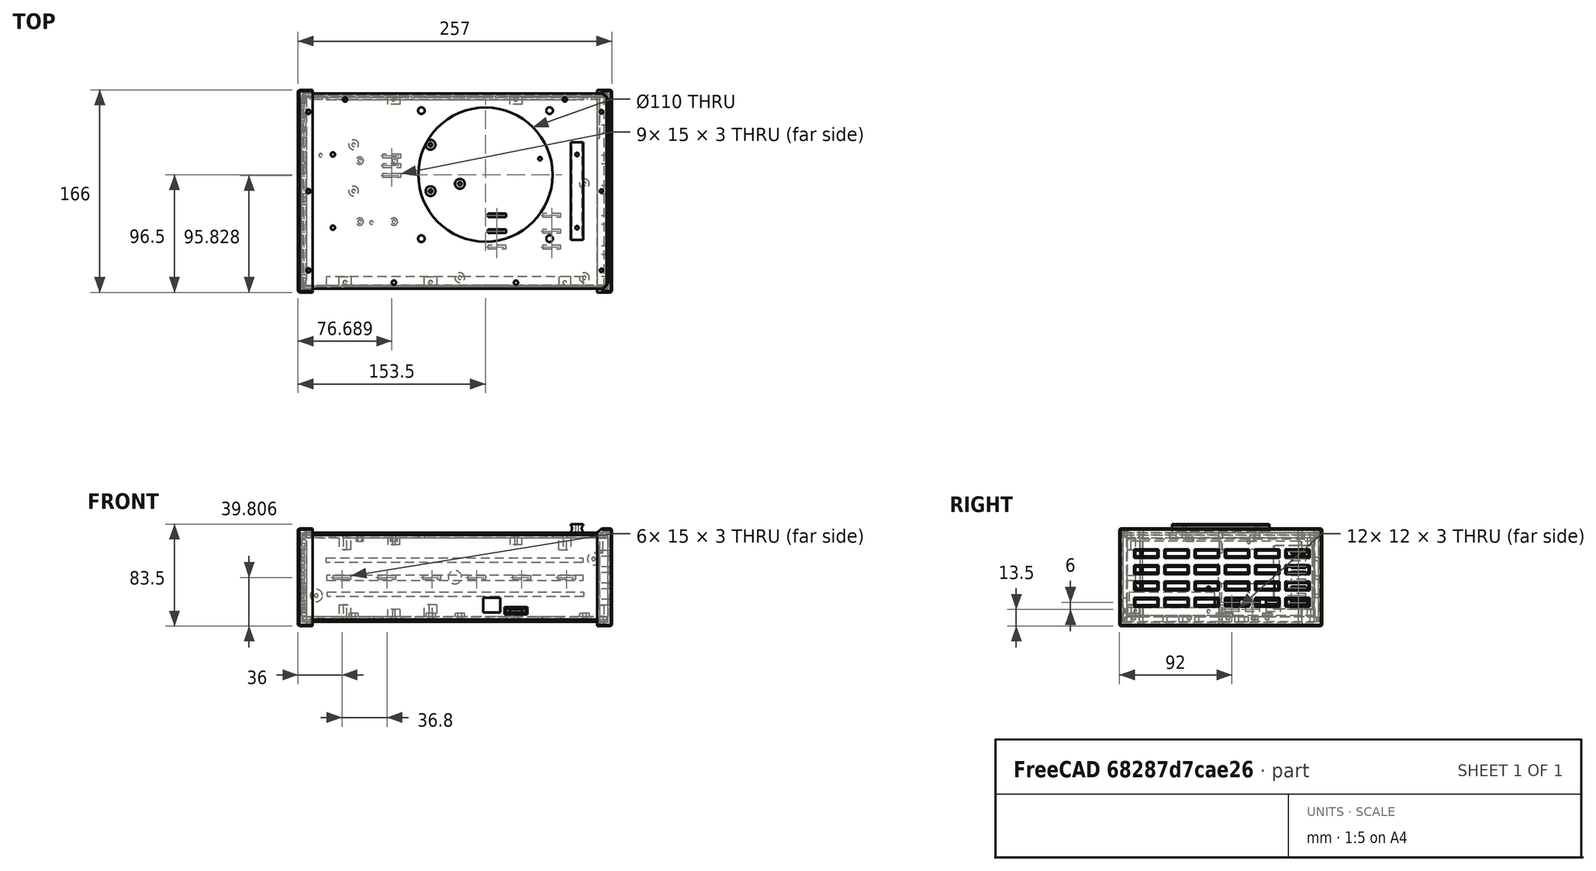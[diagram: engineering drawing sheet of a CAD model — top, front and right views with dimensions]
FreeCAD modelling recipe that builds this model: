
FCSTD DOCUMENT  (FreeCAD 0.19R)
Label: PowerBox
License: All rights reserved
LicenseURL: http://en.wikipedia.org/wiki/All_rights_reserved
objects: Sketcher::SketchObject×48, PartDesign::Pocket×28, PartDesign::Pad×18, PartDesign::Chamfer×9, Mesh::Feature×8, PartDesign::Body×7, PartDesign::Mirrored×5, PartDesign::LinearPattern×3, PartDesign::MultiTransform×2
note: 175 computed .brp shape members not serialized (recipe doc carries the construction recipe); baked Part::Feature solids carry a one-line shape summary decoded from their .brp

FEATURE [Sketcher::SketchObject] Sketch
  FullyConstrained = false
  MapMode = 5
  Support = -> [XY_Plane]
  sketch-geometry (52):
    g0: LineSegment StartX=-86.5424 StartY=49.9671 StartZ=0 EndX=-14.5424 EndY=49.9671 EndZ=0
    g1: LineSegment StartX=-14.5424 StartY=49.9671 StartZ=0 EndX=-14.5424 EndY=4.96706 EndZ=0
    g2: LineSegment StartX=-14.5424 StartY=4.96706 StartZ=0 EndX=-86.5424 EndY=4.96706 EndZ=0
    g3: LineSegment StartX=-86.5424 StartY=4.96706 StartZ=0 EndX=-86.5424 EndY=49.9671 EndZ=0
    g4: LineSegment StartX=25.4911 StartY=34.3238 StartZ=0 EndX=135.491 EndY=34.3238 EndZ=0
    g5: LineSegment StartX=135.491 StartY=34.3238 StartZ=0 EndX=135.491 EndY=-50.6762 EndZ=0
    g6: LineSegment StartX=135.491 StartY=-50.6762 StartZ=0 EndX=25.4911 EndY=-50.6762 EndZ=0
    g7: LineSegment StartX=25.4911 StartY=-50.6762 StartZ=0 EndX=25.4911 EndY=34.3238 EndZ=0
    g8: LineSegment StartX=49.4911 StartY=-35.6762 StartZ=0 EndX=61.4911 EndY=-35.6762 EndZ=0
    g9: LineSegment StartX=61.4911 StartY=-35.6762 StartZ=0 EndX=61.4911 EndY=-50.6762 EndZ=0
    g10: LineSegment StartX=61.4911 StartY=-50.6762 StartZ=0 EndX=49.4911 EndY=-50.6762 EndZ=0
    g11: LineSegment StartX=49.4911 StartY=-50.6762 StartZ=0 EndX=49.4911 EndY=-35.6762 EndZ=0
    g12: LineSegment StartX=67.9911 StartY=-35.6762 StartZ=0 EndX=82.9911 EndY=-35.6762 EndZ=0
    g13: LineSegment StartX=82.9911 StartY=-35.6762 StartZ=0 EndX=82.9911 EndY=-50.6762 EndZ=0
    g14: LineSegment StartX=82.9911 StartY=-50.6762 StartZ=0 EndX=67.9911 EndY=-50.6762 EndZ=0
    g15: LineSegment StartX=67.9911 StartY=-50.6762 StartZ=0 EndX=67.9911 EndY=-35.6762 EndZ=0
    g16: Circle CenterX=29.5661 CenterY=29.9738 CenterZ=0 NormalX=0 NormalY=0 NormalZ=1 AngleXU=0 Radius=1.75
    g17: Circle CenterX=131.416 CenterY=29.9738 CenterZ=0 NormalX=0 NormalY=0 NormalZ=1 AngleXU=0 Radius=1.75
    g18: Circle CenterX=29.5661 CenterY=-46.3262 CenterZ=0 NormalX=0 NormalY=0 NormalZ=1 AngleXU=0 Radius=1.75
    g19: Circle CenterX=131.416 CenterY=-46.3262 CenterZ=0 NormalX=0 NormalY=0 NormalZ=1 AngleXU=0 Radius=1.75
    g20: Circle CenterX=-82.0424 CenterY=46.4671 CenterZ=0 NormalX=0 NormalY=0 NormalZ=1 AngleXU=0 Radius=1.75
    g21: Circle CenterX=-19.0424 CenterY=46.4671 CenterZ=0 NormalX=0 NormalY=0 NormalZ=1 AngleXU=0 Radius=1.75
    g22: Circle CenterX=-82.0424 CenterY=8.46706 CenterZ=0 NormalX=0 NormalY=0 NormalZ=1 AngleXU=0 Radius=1.75
    g23: Circle CenterX=-19.0424 CenterY=8.46706 CenterZ=0 NormalX=0 NormalY=0 NormalZ=1 AngleXU=0 Radius=1.75
    g24: LineSegment StartX=80.4911 StartY=34.3238 StartZ=0 EndX=80.4911 EndY=-50.6762 EndZ=0
    g25: LineSegment StartX=25.4911 StartY=-8.17615 StartZ=0 EndX=135.491 EndY=-8.17615 EndZ=0
    g26: LineSegment StartX=-50.5424 StartY=4.96706 StartZ=0 EndX=-50.5424 EndY=49.9671 EndZ=0
    g27: LineSegment StartX=-86.5424 StartY=27.4671 StartZ=0 EndX=-14.5424 EndY=27.4671 EndZ=0
    g28: LineSegment StartX=-24.5424 StartY=17.4671 StartZ=0 EndX=-14.5424 EndY=17.4671 EndZ=0
    g29: LineSegment StartX=-14.5424 StartY=17.4671 StartZ=0 EndX=-14.5424 EndY=27.4671 EndZ=0
    g30: LineSegment StartX=-14.5424 StartY=27.4671 StartZ=0 EndX=-24.5424 EndY=27.4671 EndZ=0
    g31: LineSegment StartX=-24.5424 StartY=27.4671 StartZ=0 EndX=-24.5424 EndY=17.4671 EndZ=0
    g32: LineSegment StartX=-81.5424 StartY=32.4671 StartZ=0 EndX=-71.5424 EndY=32.4671 EndZ=0
    g33: LineSegment StartX=-71.5424 StartY=32.4671 StartZ=0 EndX=-71.5424 EndY=22.4671 EndZ=0
    g34: LineSegment StartX=-71.5424 StartY=22.4671 StartZ=0 EndX=-81.5424 EndY=22.4671 EndZ=0
    g35: LineSegment StartX=-81.5424 StartY=22.4671 StartZ=0 EndX=-81.5424 EndY=32.4671 EndZ=0
    g36: LineSegment StartX=-100.377 StartY=89.1721 StartZ=0 EndX=139.623 EndY=89.1721 EndZ=0
    g37: LineSegment StartX=139.623 StartY=89.1721 StartZ=0 EndX=139.623 EndY=59.1721 EndZ=0
    g38: LineSegment StartX=139.623 StartY=59.1721 StartZ=0 EndX=-100.377 EndY=59.1721 EndZ=0
    g39: LineSegment StartX=-100.377 StartY=59.1721 StartZ=0 EndX=-100.377 EndY=89.1721 EndZ=0
    g40: LineSegment StartX=-96.5075 StartY=-1.10795 StartZ=0 EndX=3.49248 EndY=-1.10795 EndZ=0
    g41: LineSegment StartX=3.49248 StartY=-1.10795 StartZ=0 EndX=3.49248 EndY=-54.108 EndZ=0
    g42: LineSegment StartX=3.49248 StartY=-54.108 StartZ=0 EndX=-96.5075 EndY=-54.108 EndZ=0
    g43: LineSegment StartX=-96.5075 StartY=-54.108 StartZ=0 EndX=-96.5075 EndY=-1.10795 EndZ=0
    g44: LineSegment StartX=40.4911 StartY=31.3238 StartZ=0 EndX=120.491 EndY=31.3238 EndZ=0
    g45: LineSegment StartX=120.491 StartY=31.3238 StartZ=0 EndX=120.491 EndY=21.3238 EndZ=0
    g46: LineSegment StartX=120.491 StartY=21.3238 StartZ=0 EndX=40.4911 EndY=21.3238 EndZ=0
    g47: LineSegment StartX=40.4911 StartY=21.3238 StartZ=0 EndX=40.4911 EndY=31.3238 EndZ=0
    g48: LineSegment StartX=-125 StartY=80 StartZ=0 EndX=125 EndY=80 EndZ=0
    g49: LineSegment StartX=125 StartY=80 StartZ=0 EndX=125 EndY=-80 EndZ=0
    g50: LineSegment StartX=125 StartY=-80 StartZ=0 EndX=-125 EndY=-80 EndZ=0
    g51: LineSegment StartX=-125 StartY=-80 StartZ=0 EndX=-125 EndY=80 EndZ=0
  constraints (138):
    c: Coincident(g0,g1)
    c: Coincident(g1,g2)
    c: Coincident(g2,g3)
    c: Coincident(g3,g0)
    c: Horizontal(g0)
    c: Horizontal(g2)
    c: Vertical(g1)
    c: Vertical(g3)
    c: Distance(g0) = 72
    c: Distance(g1) = 45
    c: Coincident(g4,g5)
    c: Coincident(g5,g6)
    c: Coincident(g6,g7)
    c: Coincident(g7,g4)
    c: Horizontal(g4)
    c: Horizontal(g6)
    c: Vertical(g5)
    c: Vertical(g7)
    c: Distance(g4) = 110
    c: Distance(g5) = 85
    c: Coincident(g8,g9)
    c: Coincident(g9,g10)
    c: Coincident(g10,g11)
    c: Coincident(g11,g8)
    c: Horizontal(g8)
    c: Horizontal(g10)
    c: Vertical(g9)
    c: Vertical(g11)
    c: Coincident(g12,g13)
    c: Coincident(g13,g14)
    c: Coincident(g14,g15)
    c: Coincident(g15,g12)
    c: Horizontal(g12)
    c: Horizontal(g14)
    c: Vertical(g13)
    c: Vertical(g15)
    c: Distance(g6,g10) = 24
    c: Distance(g9,g6) = 36
    c: PointOnObject(g9,g6)
    c: DistanceX(g6,g14) = 42.5
    c: PointOnObject(g14,g6)
    c: Distance(g13,g6) = 57.5
    c: Equal(g9,g15)
    c: Distance(g13) = 15
    c: Diameter(g20) = 3.5
    c: Equal(g20,g22)
    c: Equal(g20,g21)
    c: Equal(g20,g23)
    c: Equal(g20,g16)
    c: Equal(g20,g18)
    c: Equal(g20,g17)
    c: Equal(g20,g19)
    c: PointOnObject(g24,g6)
    c: Vertical(g24)
    c: PointOnObject(g25,g7)
    c: Horizontal(g25)
    c: PointOnObject(g26,g2)
    c: PointOnObject(g27,g3)
    c: Horizontal(g27)
    c: Vertical(g26)
    c: Symmetric(g0,g0,g26)
    c: Symmetric(g0,g1,g27)
    c: Symmetric(g5,g4,g25)
    c: Symmetric(g4,g4,g24)
    c: Symmetric(g17,g16,g24)
    c: Distance(g16,g17) = 101.85
    c: Symmetric(g19,g17,g25)
    c: Distance(g17,g19) = 76.3
    c: DistanceX(g16,g18) = 0
    c: DistanceY(g19,g18) = 0
    c: Symmetric(g20,g21,g26)
    c: Symmetric(g23,g21,g27)
    c: Symmetric(g22,g20,g27)
    c: Distance(g21,g23) = 38
    c: Distance(g21,g20) = 63
    c: Coincident(g28,g29)
    c: Coincident(g29,g30)
    c: Coincident(g30,g31)
    c: Coincident(g31,g28)
    c: Horizontal(g28)
    c: Horizontal(g30)
    c: Vertical(g29)
    c: Vertical(g31)
    c: Coincident(g32,g33)
    c: Coincident(g33,g34)
    c: Coincident(g34,g35)
    c: Coincident(g35,g32)
    c: Horizontal(g32)
    c: Horizontal(g34)
    c: Vertical(g35)
    c: Symmetric(g33,g32,g27)
    c: Distance(g33) = 10
    c: Distance(g32) = 10
    c: Distance(g32,g3) = 5
    c: Coincident(g29,g27)
    c: Distance(g28) = 10
    c: Distance(g31) = 10
    c: Coincident(g36,g37)
    c: Coincident(g37,g38)
    c: Coincident(g38,g39)
    c: Coincident(g39,g36)
    c: Horizontal(g36)
    c: Horizontal(g38)
    c: Vertical(g37)
    c: Vertical(g39)
    c: Distance(g36) = 240
    c: Distance(g37) = 30
    c: Coincident(g40,g41)
    c: Coincident(g41,g42)
    c: Coincident(g42,g43)
    c: Coincident(g43,g40)
    c: Horizontal(g40)
    c: Horizontal(g42)
    c: Vertical(g41)
    c: Vertical(g43)
    c: Distance(g40) = 100
    c: Distance(g41) = 53
    c: Coincident(g44,g45)
    c: Coincident(g45,g46)
    c: Coincident(g46,g47)
    c: Coincident(g47,g44)
    c: Horizontal(g46)
    c: Vertical(g45)
    c: Vertical(g47)
    c: Symmetric(g44,g44,g24)
    c: Distance(g45) = 10
    c: Distance(g44) = 80
    c: Distance(g44,g4) = 3
    c: Coincident(g48,g49)
    c: Coincident(g49,g50)
    c: Coincident(g50,g51)
    c: Coincident(g51,g48)
    c: Horizontal(g50)
    c: Vertical(g49)
    c: Distance(g49) = 160
    c: Distance(g48) = 250
    c: Symmetric(g48,g48,g-2)
    c: Symmetric(g50,g48,g-1)
FEATURE [PartDesign::Pad] Pad
  Direction = (1,1,1)
  Length = 4
  Length2 = 100
  Profile = -> Sketch
  Type = 0
FEATURE [Sketcher::SketchObject] Sketch001
  FullyConstrained = false
  MapMode = 5
  Placement = pos=(0,0,4) rot=(0,0,1;0rad)
  Support = -> [Pad]
  sketch-geometry (60):
    g0: LineSegment StartX=-87.5 StartY=41.4585 StartZ=0 EndX=-15.5 EndY=41.4585 EndZ=0
    g1: LineSegment StartX=-15.5 StartY=41.4585 StartZ=0 EndX=-15.5 EndY=-3.45847 EndZ=0
    g2: LineSegment StartX=-15.5 StartY=-3.45847 StartZ=0 EndX=-87.5 EndY=-3.45847 EndZ=0
    g3: LineSegment StartX=-87.5 StartY=-3.45847 StartZ=0 EndX=-87.5 EndY=41.4585 EndZ=0
    g4: LineSegment StartX=0 StartY=10 StartZ=0 EndX=110 EndY=10 EndZ=0
    g5: LineSegment StartX=110 StartY=10 StartZ=0 EndX=110 EndY=-75 EndZ=0
    g6: LineSegment StartX=110 StartY=-75 StartZ=0 EndX=0 EndY=-75 EndZ=0
    g7: LineSegment StartX=0 StartY=-75 StartZ=0 EndX=0 EndY=10 EndZ=0
    g8: LineSegment StartX=24 StartY=-60 StartZ=0 EndX=36 EndY=-60 EndZ=0
    g9: LineSegment StartX=36 StartY=-60 StartZ=0 EndX=36 EndY=-75 EndZ=0
    g10: LineSegment StartX=36 StartY=-75 StartZ=0 EndX=24 EndY=-75 EndZ=0
    g11: LineSegment StartX=24 StartY=-75 StartZ=0 EndX=24 EndY=-60 EndZ=0
    g12: LineSegment StartX=42.5 StartY=-60 StartZ=0 EndX=57.5 EndY=-60 EndZ=0
    g13: LineSegment StartX=57.5 StartY=-60 StartZ=0 EndX=57.5 EndY=-75 EndZ=0
    g14: LineSegment StartX=57.5 StartY=-75 StartZ=0 EndX=42.5 EndY=-75 EndZ=0
    g15: LineSegment StartX=42.5 StartY=-75 StartZ=0 EndX=42.5 EndY=-60 EndZ=0
    g16: Circle CenterX=4 CenterY=6 CenterZ=0 NormalX=0 NormalY=0 NormalZ=1 AngleXU=0 Radius=1.75
    g17: Circle CenterX=106 CenterY=6 CenterZ=0 NormalX=0 NormalY=0 NormalZ=1 AngleXU=0 Radius=1.75
    g18: Circle CenterX=4 CenterY=-71 CenterZ=0 NormalX=0 NormalY=0 NormalZ=1 AngleXU=0 Radius=1.75
    g19: Circle CenterX=106 CenterY=-71 CenterZ=0 NormalX=0 NormalY=0 NormalZ=1 AngleXU=0 Radius=1.75
    g20: Circle CenterX=-83 CenterY=38 CenterZ=0 NormalX=0 NormalY=0 NormalZ=1 AngleXU=0 Radius=1.75
    g21: Circle CenterX=-20 CenterY=38 CenterZ=0 NormalX=0 NormalY=0 NormalZ=1 AngleXU=0 Radius=1.75
    g22: Circle CenterX=-83 CenterY=-3.5e-15 CenterZ=0 NormalX=0 NormalY=0 NormalZ=1 AngleXU=0 Radius=1.75
    g23: Circle CenterX=-20 CenterY=0 CenterZ=0 NormalX=0 NormalY=0 NormalZ=1 AngleXU=0 Radius=1.75
    g24: LineSegment StartX=55 StartY=10 StartZ=0 EndX=55 EndY=-75 EndZ=0
    g25: LineSegment StartX=3.9e-15 StartY=-32.5 StartZ=0 EndX=110 EndY=-32.5 EndZ=0
    g26: LineSegment StartX=-51.5 StartY=-3.45847 StartZ=0 EndX=-51.5 EndY=41.4585 EndZ=0
    g27: LineSegment StartX=-87.5 StartY=19 StartZ=0 EndX=-15.5 EndY=19 EndZ=0
    g28: LineSegment StartX=-25.5 StartY=9 StartZ=0 EndX=-15.5 EndY=9 EndZ=0
    g29: LineSegment StartX=-15.5 StartY=9 StartZ=0 EndX=-15.5 EndY=19 EndZ=0
    g30: LineSegment StartX=-15.5 StartY=19 StartZ=0 EndX=-25.5 EndY=19 EndZ=0
    g31: LineSegment StartX=-25.5 StartY=19 StartZ=0 EndX=-25.5 EndY=9 EndZ=0
    g32: LineSegment StartX=-82.5 StartY=24 StartZ=0 EndX=-72.5 EndY=24 EndZ=0
    g33: LineSegment StartX=-72.5 StartY=24 StartZ=0 EndX=-72.5 EndY=14 EndZ=0
    g34: LineSegment StartX=-72.5 StartY=14 StartZ=0 EndX=-82.5 EndY=14 EndZ=0
    g35: LineSegment StartX=-82.5 StartY=14 StartZ=0 EndX=-82.5 EndY=24 EndZ=0
    g36: LineSegment StartX=-120.694 StartY=75.1603 StartZ=0 EndX=119.306 EndY=75.1603 EndZ=0
    g37: LineSegment StartX=119.306 StartY=75.1603 StartZ=0 EndX=119.306 EndY=45.1603 EndZ=0
    g38: LineSegment StartX=119.306 StartY=45.1603 StartZ=0 EndX=-120.694 EndY=45.1603 EndZ=0
    g39: LineSegment StartX=-120.694 StartY=45.1603 StartZ=0 EndX=-120.694 EndY=75.1603 EndZ=0
    g40: LineSegment StartX=-121.323 StartY=-10.2354 StartZ=0 EndX=-21.3228 EndY=-10.2354 EndZ=0
    g41: LineSegment StartX=-21.3228 StartY=-10.2354 StartZ=0 EndX=-21.3228 EndY=-63.2354 EndZ=0
    g42: LineSegment StartX=-21.3228 StartY=-63.2354 StartZ=0 EndX=-121.323 EndY=-63.2354 EndZ=0
    g43: LineSegment StartX=-121.323 StartY=-63.2354 StartZ=0 EndX=-121.323 EndY=-10.2354 EndZ=0
    g44: LineSegment StartX=15 StartY=7 StartZ=0 EndX=95 EndY=7 EndZ=0
    g45: LineSegment StartX=95 StartY=7 StartZ=0 EndX=95 EndY=-3 EndZ=0
    g46: LineSegment StartX=95 StartY=-3 StartZ=0 EndX=15 EndY=-3 EndZ=0
    g47: LineSegment StartX=15 StartY=-3 StartZ=0 EndX=15 EndY=7 EndZ=0
    g48: LineSegment StartX=-125.107 StartY=95.65 StartZ=0 EndX=124.893 EndY=95.65 EndZ=0
    g49: LineSegment StartX=124.893 StartY=95.65 StartZ=0 EndX=124.893 EndY=-80.1453 EndZ=0
    g50: LineSegment StartX=124.893 StartY=-80.1453 StartZ=0 EndX=-125.107 EndY=-80.1453 EndZ=0
    g51: LineSegment StartX=-125.107 StartY=-80.1453 StartZ=0 EndX=-125.107 EndY=95.65 EndZ=0
    g52: Circle CenterX=4 CenterY=6 CenterZ=0 NormalX=0 NormalY=0 NormalZ=1 AngleXU=0 Radius=4
    g53: Circle CenterX=106 CenterY=6 CenterZ=0 NormalX=0 NormalY=0 NormalZ=1 AngleXU=0 Radius=4
    g54: Circle CenterX=106 CenterY=-71 CenterZ=0 NormalX=0 NormalY=0 NormalZ=1 AngleXU=0 Radius=4
    g55: Circle CenterX=4 CenterY=-71 CenterZ=0 NormalX=0 NormalY=0 NormalZ=1 AngleXU=0 Radius=4
    g56: Circle CenterX=-83 CenterY=38 CenterZ=0 NormalX=0 NormalY=0 NormalZ=1 AngleXU=0 Radius=4
    g57: Circle CenterX=-20 CenterY=38 CenterZ=0 NormalX=0 NormalY=0 NormalZ=1 AngleXU=0 Radius=4
    g58: Circle CenterX=-20 CenterY=0 CenterZ=0 NormalX=0 NormalY=0 NormalZ=1 AngleXU=0 Radius=4
    g59: Circle CenterX=-83 CenterY=-3.5e-15 CenterZ=0 NormalX=0 NormalY=0 NormalZ=1 AngleXU=0 Radius=4
  constraints (156):
    c: Coincident(g0,g1)
    c: Coincident(g1,g2)
    c: Coincident(g2,g3)
    c: Coincident(g3,g0)
    c: Horizontal(g0)
    c: Horizontal(g2)
    c: Vertical(g1)
    c: Vertical(g3)
    c: Distance(g0) = 72
    c: Coincident(g4,g5)
    c: Coincident(g5,g6)
    c: Coincident(g6,g7)
    c: Coincident(g7,g4)
    c: Horizontal(g4)
    c: Horizontal(g6)
    c: Vertical(g5)
    c: Vertical(g7)
    c: Distance(g4) = 110
    c: Distance(g5) = 85
    c: Coincident(g8,g9)
    c: Coincident(g9,g10)
    c: Coincident(g10,g11)
    c: Coincident(g11,g8)
    c: Horizontal(g8)
    c: Horizontal(g10)
    c: Vertical(g9)
    c: Vertical(g11)
    c: Coincident(g12,g13)
    c: Coincident(g13,g14)
    c: Coincident(g14,g15)
    c: Coincident(g15,g12)
    c: Horizontal(g12)
    c: Horizontal(g14)
    c: Vertical(g13)
    c: Vertical(g15)
    c: Distance(g6,g10) = 24
    c: Distance(g9,g6) = 36
    c: PointOnObject(g9,g6)
    c: DistanceX(g6,g14) = 42.5
    c: PointOnObject(g14,g6)
    c: Distance(g13,g6) = 57.5
    c: Equal(g9,g15)
    c: Distance(g13) = 15
    c: Diameter(g20) = 3.5
    c: Equal(g20,g22)
    c: Equal(g20,g21)
    c: Equal(g20,g23)
    c: Equal(g20,g16)
    c: Equal(g20,g18)
    c: Equal(g20,g17)
    c: Equal(g20,g19)
    c: PointOnObject(g24,g6)
    c: Vertical(g24)
    c: PointOnObject(g25,g7)
    c: Horizontal(g25)
    c: PointOnObject(g26,g2)
    c: PointOnObject(g27,g3)
    c: Horizontal(g27)
    c: Vertical(g26)
    c: Symmetric(g0,g0,g26)
    c: Symmetric(g0,g1,g27)
    c: Symmetric(g5,g4,g25)
    c: Symmetric(g4,g4,g24)
    c: Symmetric(g17,g16,g24)
    c: Distance(g16,g17) = 102
    c: Symmetric(g19,g17,g25)
    c: DistanceX(g16,g18) = 0
    c: DistanceY(g19,g18) = 0
    c: Symmetric(g20,g21,g26)
    c: Symmetric(g23,g21,g27)
    c: Symmetric(g22,g20,g27)
    c: Distance(g21,g23) = 38
    c: Distance(g21,g20) = 63
    c: Coincident(g28,g29)
    c: Coincident(g29,g30)
    c: Coincident(g30,g31)
    c: Coincident(g31,g28)
    c: Horizontal(g28)
    c: Horizontal(g30)
    c: Vertical(g29)
    c: Vertical(g31)
    c: Coincident(g32,g33)
    c: Coincident(g33,g34)
    c: Coincident(g34,g35)
    c: Coincident(g35,g32)
    c: Horizontal(g32)
    c: Horizontal(g34)
    c: Vertical(g35)
    c: Symmetric(g33,g32,g27)
    c: Distance(g33) = 10
    c: Distance(g32) = 10
    c: Distance(g32,g3) = 5
    c: Coincident(g29,g27)
    c: Distance(g28) = 10
    c: Distance(g31) = 10
    c: Coincident(g36,g37)
    c: Coincident(g37,g38)
    c: Coincident(g38,g39)
    c: Coincident(g39,g36)
    c: Horizontal(g36)
    c: Horizontal(g38)
    c: Vertical(g37)
    c: Vertical(g39)
    c: Distance(g36) = 240
    c: Distance(g37) = 30
    c: Coincident(g40,g41)
    c: Coincident(g41,g42)
    c: Coincident(g42,g43)
    c: Coincident(g43,g40)
    c: Horizontal(g40)
    c: Horizontal(g42)
    c: Vertical(g41)
    c: Vertical(g43)
    c: Distance(g40) = 100
    c: Distance(g41) = 53
    c: Coincident(g44,g45)
    c: Coincident(g45,g46)
    c: Coincident(g46,g47)
    c: Coincident(g47,g44)
    c: Horizontal(g46)
    c: Vertical(g45)
    c: Vertical(g47)
    c: Symmetric(g44,g44,g24)
    c: Distance(g45) = 10
    c: Distance(g44) = 80
    c: Distance(g44,g4) = 3
    c: Coincident(g48,g49)
    c: Coincident(g49,g50)
    c: Coincident(g50,g51)
    c: Coincident(g51,g48)
    c: Horizontal(g48)
    c: Horizontal(g50)
    c: Vertical(g49)
    c: Vertical(g51)
    c: Distance(g48) = 250
    c: Coincident(g52,g16)
    c: Coincident(g53,g17)
    c: Coincident(g54,g19)
    c: Coincident(g55,g18)
    c: Coincident(g56,g20)
    c: Coincident(g57,g21)
    c: Coincident(g58,g23)
    c: Coincident(g59,g22)
    c: Diameter(g54) = 8
    c: Equal(g54,g53)
    c: Equal(g54,g52)
    c: Equal(g54,g55)
    c: Equal(g54,g58)
    c: Equal(g54,g57)
    c: Equal(g54,g56)
    c: Equal(g54,g59)
    c: DistanceY(g5) = -75
    c: DistanceX(g5) = 110
    c: DistanceX(g57) = -20
    c: Distance(g53,g54) = 77
    c: PointOnObject(g58,g-1)
FEATURE [Sketcher::SketchObject] Sketch003  label="reference"
  FullyConstrained = false
  MapMode = 5
  Placement = pos=(0,0,0) rot=(0.57735,0.57735,0.57735;2.0944rad)
  Support = -> [YZ_Plane001]
  sketch-geometry (4):
    g0: LineSegment StartX=-80.0312 StartY=59.7173 StartZ=0 EndX=-51.0312 EndY=59.7173 EndZ=0
    g1: LineSegment StartX=-51.0312 StartY=59.7173 StartZ=0 EndX=-51.0312 EndY=11.7173 EndZ=0
    g2: LineSegment StartX=-51.0312 StartY=11.7173 StartZ=0 EndX=-80.0312 EndY=11.7173 EndZ=0
    g3: LineSegment StartX=-80.0312 StartY=11.7173 StartZ=0 EndX=-80.0312 EndY=59.7173 EndZ=0
  constraints (10):
    c: Coincident(g0,g1)
    c: Coincident(g1,g2)
    c: Coincident(g2,g3)
    c: Coincident(g3,g0)
    c: Horizontal(g0)
    c: Horizontal(g2)
    c: Vertical(g1)
    c: Vertical(g3)
    c: Distance(g0) = 29
    c: Distance(g3) = 48
FEATURE [PartDesign::Pad] Pad001
  BaseFeature = -> Pad
  Direction = (1,1,1)
  Length = 3
  Length2 = 100
  Profile = -> Sketch001
  Type = 0
FEATURE [Sketcher::SketchObject] Sketch002
  ExternalGeometry = -> [Pad001]
  FullyConstrained = true
  MapMode = 5
  Placement = pos=(0,0,7) rot=(0,0,1;0rad)
  sketch-geometry (8):
    g0: Circle CenterX=-83 CenterY=38 CenterZ=0 NormalX=0 NormalY=0 NormalZ=1 AngleXU=0 Radius=1.4
    g1: Circle CenterX=-20 CenterY=38 CenterZ=0 NormalX=0 NormalY=0 NormalZ=1 AngleXU=0 Radius=1.4
    g2: Circle CenterX=-83 CenterY=-3.5e-15 CenterZ=0 NormalX=0 NormalY=0 NormalZ=1 AngleXU=0 Radius=1.4
    g3: Circle CenterX=-20 CenterY=0 CenterZ=0 NormalX=0 NormalY=0 NormalZ=1 AngleXU=0 Radius=1.4
    g4: Circle CenterX=4 CenterY=6 CenterZ=0 NormalX=0 NormalY=0 NormalZ=1 AngleXU=0 Radius=1.4
    g5: Circle CenterX=106 CenterY=6 CenterZ=0 NormalX=0 NormalY=0 NormalZ=1 AngleXU=0 Radius=1.4
    g6: Circle CenterX=106 CenterY=-71 CenterZ=0 NormalX=0 NormalY=0 NormalZ=1 AngleXU=0 Radius=1.4
    g7: Circle CenterX=4 CenterY=-71 CenterZ=0 NormalX=0 NormalY=0 NormalZ=1 AngleXU=0 Radius=1.4
  constraints (12):
    c: Diameter(g0) = 2.8
    c: Equal(g0,g2)
    c: Equal(g0,g1)
    c: Equal(g0, g3-g7) x5
    c: Coincident(g7,g-10)
    c: Coincident(g4,g-7)
    c: Coincident(g5,g-8)
    c: Coincident(g6,g-9)
    c: Coincident(g-3,g0)
    c: Coincident(g2,g-6)
    c: Coincident(g1,g-4)
    c: Coincident(g3,g-5)
FEATURE [PartDesign::Pocket] Pocket
  BaseFeature = -> Pad001
  Length = 5
  Length2 = 100
  Profile = -> Sketch002
  Type = 0
FEATURE [Sketcher::SketchObject] Sketch004  label="MainPad"
  FullyConstrained = true
  MapMode = 5
  Placement = pos=(0,0,0) rot=(0.57735,0.57735,0.57735;2.0944rad)
  Support = -> [YZ_Plane001]
  sketch-geometry (4):
    g0: LineSegment StartX=-83 StartY=40 StartZ=0 EndX=83 EndY=40 EndZ=0
    g1: LineSegment StartX=83 StartY=40 StartZ=0 EndX=83 EndY=-40 EndZ=0
    g2: LineSegment StartX=83 StartY=-40 StartZ=0 EndX=-83 EndY=-40 EndZ=0
    g3: LineSegment StartX=-83 StartY=-40 StartZ=0 EndX=-83 EndY=40 EndZ=0
  constraints (10):
    c: Coincident(g0,g1)
    c: Coincident(g1,g2)
    c: Coincident(g2,g3)
    c: Coincident(g3,g0)
    c: Horizontal(g0)
    c: Vertical(g3)
    c: Symmetric(g1,g2,g-2)
    c: Distance(g2) = 166
    c: Distance(g1) = 80
    c: Symmetric(g1,g0,g-1)
FEATURE [PartDesign::Pad] Pad002
  Direction = (1,1,1)
  Length = 12
  Length2 = 100
  Placement = pos=(0,0,0) rot=(0.57735,0.57735,0.57735;2.0944rad)
  Profile = -> Sketch004
  Type = 0
FEATURE [Sketcher::SketchObject] Sketch005  label="MainPocket"
  FullyConstrained = true
  MapMode = 5
  Placement = pos=(0,0,0) rot=(0.57735,0.57735,-0.57735;4.18879rad)
  Support = -> [Pad002]
  sketch-geometry (8):
    g0: LineSegment StartX=-80.25 StartY=36.75 StartZ=0 EndX=80.25 EndY=36.75 EndZ=0
    g1: LineSegment StartX=80.25 StartY=36.75 StartZ=0 EndX=80.25 EndY=-36.75 EndZ=0
    g2: LineSegment StartX=80.25 StartY=-36.75 StartZ=0 EndX=-80.25 EndY=-36.75 EndZ=0
    g3: LineSegment StartX=-80.25 StartY=-36.75 StartZ=0 EndX=-80.25 EndY=36.75 EndZ=0
    g4: LineSegment StartX=-77 StartY=32 StartZ=0 EndX=77 EndY=32 EndZ=0
    g5: LineSegment StartX=77 StartY=32 StartZ=0 EndX=77 EndY=-32 EndZ=0
    g6: LineSegment StartX=77 StartY=-32 StartZ=0 EndX=-77 EndY=-32 EndZ=0
    g7: LineSegment StartX=-77 StartY=-32 StartZ=0 EndX=-77 EndY=32 EndZ=0
  constraints (22):
    c: Coincident(g0,g1)
    c: Coincident(g1,g2)
    c: Coincident(g2,g3)
    c: Coincident(g3,g0)
    c: Horizontal(g0)
    c: Horizontal(g2)
    c: Vertical(g1)
    c: Vertical(g3)
    c: Distance(g0) = 160.5
    c: Distance(g1) = 73.5
    c: Symmetric(g0,g2,g-1)
    c: Coincident(g4,g5)
    c: Coincident(g5,g6)
    c: Coincident(g6,g7)
    c: Coincident(g7,g4)
    c: Horizontal(g4)
    c: Horizontal(g6)
    c: Vertical(g5)
    c: Vertical(g7)
    c: Distance(g7) = 64
    c: Symmetric(g4,g6,g-1)
    c: Distance(g6) = 154
FEATURE [PartDesign::Pocket] Pocket001
  BaseFeature = -> Pad002
  Length = 9
  Length2 = 100
  Placement = pos=(0,0,0) rot=(0.57735,0.57735,0.57735;2.0944rad)
  Profile = -> Sketch005
  Type = 0
FEATURE [Sketcher::SketchObject] Sketch006  label="body"
  FullyConstrained = true
  MapMode = 5
  Placement = pos=(0,0,0) rot=(1,0,0;1.5708rad)
  Support = -> [XZ_Plane002]
  sketch-geometry (4):
    g0: LineSegment StartX=-125 StartY=32.5 StartZ=0 EndX=125 EndY=32.5 EndZ=0
    g1: LineSegment StartX=125 StartY=32.5 StartZ=0 EndX=125 EndY=-32.5 EndZ=0
    g2: LineSegment StartX=125 StartY=-32.5 StartZ=0 EndX=-125 EndY=-32.5 EndZ=0
    g3: LineSegment StartX=-125 StartY=-32.5 StartZ=0 EndX=-125 EndY=32.5 EndZ=0
  constraints (11):
    c: Coincident(g0,g1)
    c: Coincident(g1,g2)
    c: Coincident(g2,g3)
    c: Coincident(g3,g0)
    c: Horizontal(g0)
    c: Vertical(g1)
    c: Vertical(g3)
    c: Distance(g2) = 250
    c: Distance(g1) = 65
    c: Symmetric(g2,g0,g-1)
    c: Equal(g3,g1)
FEATURE [PartDesign::Pad] Pad003
  Direction = (1,1,1)
  Length = 3
  Length2 = 100
  Placement = pos=(0,0,0) rot=(1,0,0;1.5708rad)
  Profile = -> Sketch006
  Type = 0
FEATURE [Sketcher::SketchObject] Sketch007
  FullyConstrained = true
  MapMode = 5
  Placement = pos=(0,0,0) rot=(1,0,0;1.5708rad)
  Support = -> [XZ_Plane003]
  sketch-geometry (4):
    g0: LineSegment StartX=-125 StartY=32.5 StartZ=0 EndX=125 EndY=32.5 EndZ=0
    g1: LineSegment StartX=125 StartY=32.5 StartZ=0 EndX=125 EndY=-32.5 EndZ=0
    g2: LineSegment StartX=125 StartY=-32.5 StartZ=0 EndX=-125 EndY=-32.5 EndZ=0
    g3: LineSegment StartX=-125 StartY=-32.5 StartZ=0 EndX=-125 EndY=32.5 EndZ=0
  constraints (11):
    c: Coincident(g0,g1)
    c: Coincident(g1,g2)
    c: Coincident(g2,g3)
    c: Coincident(g3,g0)
    c: Horizontal(g0)
    c: Horizontal(g2)
    c: Vertical(g1)
    c: Vertical(g3)
    c: Distance(g1) = 65
    c: Distance(g0) = 250
    c: Symmetric(g0,g2,g-1)
FEATURE [PartDesign::Pad] Pad004
  Direction = (1,1,1)
  Length = 3
  Length2 = 100
  Placement = pos=(0,0,0) rot=(1,0,0;1.5708rad)
  Profile = -> Sketch007
  Type = 0
FEATURE [Sketcher::SketchObject] Sketch008  label="MainPad001"
  FullyConstrained = true
  MapMode = 5
  Placement = pos=(0,0,0) rot=(0.57735,0.57735,0.57735;2.0944rad)
  Support = -> [YZ_Plane004]
  sketch-geometry (4):
    g0: LineSegment StartX=-83 StartY=40 StartZ=0 EndX=83 EndY=40 EndZ=0
    g1: LineSegment StartX=83 StartY=40 StartZ=0 EndX=83 EndY=-40 EndZ=0
    g2: LineSegment StartX=83 StartY=-40 StartZ=0 EndX=-83 EndY=-40 EndZ=0
    g3: LineSegment StartX=-83 StartY=-40 StartZ=0 EndX=-83 EndY=40 EndZ=0
  constraints (11):
    c: Coincident(g0,g1)
    c: Coincident(g1,g2)
    c: Coincident(g2,g3)
    c: Coincident(g3,g0)
    c: Horizontal(g0)
    c: Horizontal(g2)
    c: Vertical(g1)
    c: Vertical(g3)
    c: Distance(g1) = 80
    c: Distance(g2) = 166
    c: Symmetric(g0,g2,g-1)
FEATURE [PartDesign::Pad] Pad005
  Direction = (1,1,1)
  Length = 12
  Length2 = 100
  Placement = pos=(0,0,0) rot=(0.57735,0.57735,0.57735;2.0944rad)
  Profile = -> Sketch008
  Type = 0
FEATURE [Sketcher::SketchObject] Sketch009  label="MainPocket001"
  FullyConstrained = true
  MapMode = 5
  Placement = pos=(12,-2.6e-15,2.6e-15) rot=(0.57735,0.57735,0.57735;2.0944rad)
  Support = -> [Pad005]
  sketch-geometry (4):
    g0: LineSegment StartX=-80.25 StartY=36.75 StartZ=0 EndX=80.25 EndY=36.75 EndZ=0
    g1: LineSegment StartX=80.25 StartY=36.75 StartZ=0 EndX=80.25 EndY=-36.75 EndZ=0
    g2: LineSegment StartX=80.25 StartY=-36.75 StartZ=0 EndX=-80.25 EndY=-36.75 EndZ=0
    g3: LineSegment StartX=-80.25 StartY=-36.75 StartZ=0 EndX=-80.25 EndY=36.75 EndZ=0
  constraints (11):
    c: Coincident(g0,g1)
    c: Coincident(g1,g2)
    c: Coincident(g2,g3)
    c: Coincident(g3,g0)
    c: Horizontal(g0)
    c: Horizontal(g2)
    c: Vertical(g1)
    c: Vertical(g3)
    c: Symmetric(g1,g0,g-1)
    c: Distance(g0) = 160.5
    c: Distance(g1) = 73.5
FEATURE [PartDesign::Pocket] Pocket002
  BaseFeature = -> Pad005
  Length = 9
  Length2 = 100
  Placement = pos=(0,0,0) rot=(0.57735,0.57735,0.57735;2.0944rad)
  Profile = -> Sketch009
  Type = 0
FEATURE [Sketcher::SketchObject] Sketch010  label="mAINpAD"
  FullyConstrained = true
  MapMode = 5
  Support = -> [XY_Plane005]
  sketch-geometry (4):
    g0: LineSegment StartX=-124 StartY=80 StartZ=0 EndX=124 EndY=80 EndZ=0
    g1: LineSegment StartX=124 StartY=80 StartZ=0 EndX=124 EndY=-80 EndZ=0
    g2: LineSegment StartX=124 StartY=-80 StartZ=0 EndX=-124 EndY=-80 EndZ=0
    g3: LineSegment StartX=-124 StartY=-80 StartZ=0 EndX=-124 EndY=80 EndZ=0
  constraints (11):
    c: Coincident(g0,g1)
    c: Coincident(g1,g2)
    c: Coincident(g2,g3)
    c: Coincident(g3,g0)
    c: Horizontal(g0)
    c: Horizontal(g2)
    c: Vertical(g1)
    c: Vertical(g3)
    c: Distance(g0) = 248
    c: Distance(g1) = 160
    c: Symmetric(g1,g0,g-1)
FEATURE [PartDesign::Pad] Pad006
  Direction = (1,1,1)
  Length = 4
  Length2 = 100
  Profile = -> Sketch010
  Type = 0
FEATURE [Sketcher::SketchObject] Sketch011  label="VentSeed"
  FullyConstrained = true
  MapMode = 5
  Placement = pos=(12,-2.6e-15,2.6e-15) rot=(0.57735,0.57735,0.57735;2.0944rad)
  Support = -> [Pocket001]
  sketch-geometry (4):
    g0: LineSegment StartX=-70 StartY=-23 StartZ=0 EndX=-52 EndY=-23 EndZ=0
    g1: LineSegment StartX=-52 StartY=-23 StartZ=0 EndX=-52 EndY=-18 EndZ=0
    g2: LineSegment StartX=-52 StartY=-18 StartZ=0 EndX=-70 EndY=-18 EndZ=0
    g3: LineSegment StartX=-70 StartY=-18 StartZ=0 EndX=-70 EndY=-23 EndZ=0
  constraints (12):
    c: Coincident(g0,g1)
    c: Coincident(g1,g2)
    c: Coincident(g2,g3)
    c: Coincident(g3,g0)
    c: Horizontal(g0)
    c: Horizontal(g2)
    c: Vertical(g1)
    c: Vertical(g3)
    c: Distance(g1) = 5
    c: Distance(g0) = 18
    c: DistanceX(g2) = -70
    c: DistanceY(g2) = -18
FEATURE [PartDesign::Pocket] Pocket003
  BaseFeature = -> Pocket001
  Length = 5
  Length2 = 100
  Placement = pos=(0,0,0) rot=(0.57735,0.57735,0.57735;2.0944rad)
  Profile = -> Sketch011
  Type = 1
FEATURE [PartDesign::LinearPattern] LinearPattern
  Direction = -> Sketch011 [H_Axis]
  Length = 124
  Occurrences = 6
  Placement = pos=(0,0,0) rot=(0.57735,0.57735,0.57735;2.0944rad)
FEATURE [PartDesign::LinearPattern] LinearPattern001
  Direction = -> Sketch011 [V_Axis]
  Length = 40
  Occurrences = 4
  Placement = pos=(0,0,0) rot=(0.57735,0.57735,0.57735;2.0944rad)
FEATURE [PartDesign::MultiTransform] MultiTransform
  BaseFeature = -> Pocket003
  Originals = -> [Pocket003]
  Placement = pos=(0,0,0) rot=(0.57735,0.57735,0.57735;2.0944rad)
  Transformations = -> [LinearPattern,LinearPattern001]
FEATURE [Sketcher::SketchObject] Sketch012  label="AllCutouts"
  ExternalGeometry = -> [Pocket002]
  FullyConstrained = false
  MapMode = 5
  Placement = pos=(0,0,0) rot=(0.57735,0.57735,-0.57735;4.18879rad)
  Support = -> [Pocket002]
  sketch-geometry (76):
    g0: LineSegment StartX=-75 StartY=24.75 StartZ=0 EndX=-5 EndY=24.75 EndZ=0
    g1: LineSegment StartX=-5 StartY=24.75 StartZ=0 EndX=-5 EndY=12.25 EndZ=0
    g2: LineSegment StartX=-5 StartY=12.25 StartZ=0 EndX=-75 EndY=12.25 EndZ=0
    g3: LineSegment StartX=-75 StartY=12.25 StartZ=0 EndX=-75 EndY=24.75 EndZ=0
    g4: LineSegment StartX=-2 StartY=5 StartZ=0 EndX=48 EndY=5 EndZ=0
    g5: LineSegment StartX=48 StartY=5 StartZ=0 EndX=48 EndY=-23 EndZ=0
    g6: LineSegment StartX=48 StartY=-23 StartZ=0 EndX=-2 EndY=-23 EndZ=0
    g7: LineSegment StartX=-2 StartY=-23 StartZ=0 EndX=-2 EndY=5 EndZ=0
    g8: Circle CenterX=23 CenterY=11 CenterZ=0 NormalX=0 NormalY=0 NormalZ=1 AngleXU=0 Radius=1.4
    g9: Circle CenterX=23 CenterY=-29 CenterZ=0 NormalX=0 NormalY=0 NormalZ=1 AngleXU=0 Radius=1.4
    g10: LineSegment StartX=-2 StartY=-9 StartZ=0 EndX=48 EndY=-9 EndZ=0
    g11: LineSegment StartX=23 StartY=5 StartZ=0 EndX=23 EndY=-23 EndZ=0
    g12: LineSegment StartX=3 StartY=28 StartZ=0 EndX=15 EndY=28 EndZ=0
    g13: LineSegment StartX=15 StartY=28 StartZ=0 EndX=15 EndY=25 EndZ=0
    g14: LineSegment StartX=15 StartY=25 StartZ=0 EndX=3 EndY=25 EndZ=0
    g15: LineSegment StartX=3 StartY=25 StartZ=0 EndX=3 EndY=28 EndZ=0
    g16: LineSegment StartX=20 StartY=28 StartZ=0 EndX=32 EndY=28 EndZ=0
    g17: LineSegment StartX=32 StartY=28 StartZ=0 EndX=32 EndY=25 EndZ=0
    g18: LineSegment StartX=32 StartY=25 StartZ=0 EndX=20 EndY=25 EndZ=0
    g19: LineSegment StartX=20 StartY=25 StartZ=0 EndX=20 EndY=28 EndZ=0
    g20: LineSegment StartX=37 StartY=28 StartZ=0 EndX=49 EndY=28 EndZ=0
    g21: LineSegment StartX=49 StartY=28 StartZ=0 EndX=49 EndY=25 EndZ=0
    g22: LineSegment StartX=49 StartY=25 StartZ=0 EndX=37 EndY=25 EndZ=0
    g23: LineSegment StartX=37 StartY=25 StartZ=0 EndX=37 EndY=28 EndZ=0
    g24: LineSegment StartX=3 StartY=22 StartZ=0 EndX=15 EndY=22 EndZ=0
    g25: LineSegment StartX=15 StartY=22 StartZ=0 EndX=15 EndY=19 EndZ=0
    g26: LineSegment StartX=15 StartY=19 StartZ=0 EndX=3 EndY=19 EndZ=0
    g27: LineSegment StartX=3 StartY=19 StartZ=0 EndX=3 EndY=22 EndZ=0
    g28: LineSegment StartX=20 StartY=22 StartZ=0 EndX=32 EndY=22 EndZ=0
    g29: LineSegment StartX=32 StartY=22 StartZ=0 EndX=32 EndY=19 EndZ=0
    g30: LineSegment StartX=32 StartY=19 StartZ=0 EndX=20 EndY=19 EndZ=0
    g31: LineSegment StartX=20 StartY=19 StartZ=0 EndX=20 EndY=22 EndZ=0
    g32: LineSegment StartX=37 StartY=22 StartZ=0 EndX=49 EndY=22 EndZ=0
    g33: LineSegment StartX=49 StartY=22 StartZ=0 EndX=49 EndY=19 EndZ=0
    g34: LineSegment StartX=49 StartY=19 StartZ=0 EndX=37 EndY=19 EndZ=0
    g35: LineSegment StartX=37 StartY=19 StartZ=0 EndX=37 EndY=22 EndZ=0
    g36: Circle CenterX=-70 CenterY=28 CenterZ=0 NormalX=0 NormalY=0 NormalZ=1 AngleXU=0 Radius=1.4
    g37: Circle CenterX=-70 CenterY=9 CenterZ=0 NormalX=0 NormalY=0 NormalZ=1 AngleXU=0 Radius=1.4
    g38: LineSegment StartX=-70 StartY=28 StartZ=0 EndX=-70 EndY=9 EndZ=0
    g39: Circle CenterX=-10 CenterY=28 CenterZ=0 NormalX=0 NormalY=0 NormalZ=1 AngleXU=0 Radius=1.4
    g40: Circle CenterX=-10 CenterY=9 CenterZ=0 NormalX=0 NormalY=0 NormalZ=1 AngleXU=0 Radius=1.4
    g41: LineSegment StartX=-10 StartY=28 StartZ=0 EndX=-10 EndY=9 EndZ=0
    g42: LineSegment StartX=57.63 StartY=22.5 StartZ=0 EndX=69.63 EndY=22.5 EndZ=0
    g43: LineSegment StartX=69.63 StartY=22.5 StartZ=0 EndX=69.63 EndY=19.5 EndZ=0
    g44: LineSegment StartX=69.63 StartY=19.5 StartZ=0 EndX=57.63 EndY=19.5 EndZ=0
    g45: LineSegment StartX=57.63 StartY=19.5 StartZ=0 EndX=57.63 EndY=22.5 EndZ=0
    g46: LineSegment StartX=57.63 StartY=16.5 StartZ=0 EndX=69.63 EndY=16.5 EndZ=0
    g47: LineSegment StartX=69.63 StartY=16.5 StartZ=0 EndX=69.63 EndY=13.5 EndZ=0
    g48: LineSegment StartX=69.63 StartY=13.5 StartZ=0 EndX=57.63 EndY=13.5 EndZ=0
    g49: LineSegment StartX=57.63 StartY=13.5 StartZ=0 EndX=57.63 EndY=16.5 EndZ=0
    g50: LineSegment StartX=57.63 StartY=10.5 StartZ=0 EndX=69.63 EndY=10.5 EndZ=0
    g51: LineSegment StartX=69.63 StartY=10.5 StartZ=0 EndX=69.63 EndY=7.5 EndZ=0
    g52: LineSegment StartX=69.63 StartY=7.5 StartZ=0 EndX=57.63 EndY=7.5 EndZ=0
    g53: LineSegment StartX=57.63 StartY=7.5 StartZ=0 EndX=57.63 EndY=10.5 EndZ=0
    g54: LineSegment StartX=57.63 StartY=4.5 StartZ=0 EndX=69.63 EndY=4.5 EndZ=0
    g55: LineSegment StartX=69.63 StartY=4.5 StartZ=0 EndX=69.63 EndY=1.5 EndZ=0
    g56: LineSegment StartX=69.63 StartY=1.5 StartZ=0 EndX=57.63 EndY=1.5 EndZ=0
    g57: LineSegment StartX=57.63 StartY=1.5 StartZ=0 EndX=57.63 EndY=4.5 EndZ=0
    g58: LineSegment StartX=57.63 StartY=-1.5 StartZ=0 EndX=69.63 EndY=-1.5 EndZ=0
    g59: LineSegment StartX=69.63 StartY=-1.5 StartZ=0 EndX=69.63 EndY=-4.5 EndZ=0
    g60: LineSegment StartX=69.63 StartY=-4.5 StartZ=0 EndX=57.63 EndY=-4.5 EndZ=0
    g61: LineSegment StartX=57.63 StartY=-4.5 StartZ=0 EndX=57.63 EndY=-1.5 EndZ=0
    g62: LineSegment StartX=57.63 StartY=-7.5 StartZ=0 EndX=69.63 EndY=-7.5 EndZ=0
    g63: LineSegment StartX=69.63 StartY=-7.5 StartZ=0 EndX=69.63 EndY=-10.5 EndZ=0
    g64: LineSegment StartX=69.63 StartY=-10.5 StartZ=0 EndX=57.63 EndY=-10.5 EndZ=0
    g65: LineSegment StartX=57.63 StartY=-10.5 StartZ=0 EndX=57.63 EndY=-7.5 EndZ=0
    g66: LineSegment StartX=57.63 StartY=-13.5 StartZ=0 EndX=69.63 EndY=-13.5 EndZ=0
    g67: LineSegment StartX=69.63 StartY=-13.5 StartZ=0 EndX=69.63 EndY=-16.5 EndZ=0
    g68: LineSegment StartX=69.63 StartY=-16.5 StartZ=0 EndX=57.63 EndY=-16.5 EndZ=0
    g69: LineSegment StartX=57.63 StartY=-16.5 StartZ=0 EndX=57.63 EndY=-13.5 EndZ=0
    g70: LineSegment StartX=57.63 StartY=-19.5 StartZ=0 EndX=69.63 EndY=-19.5 EndZ=0
    g71: LineSegment StartX=69.63 StartY=-19.5 StartZ=0 EndX=69.63 EndY=-22.5 EndZ=0
    g72: LineSegment StartX=69.63 StartY=-22.5 StartZ=0 EndX=57.63 EndY=-22.5 EndZ=0
    g73: LineSegment StartX=57.63 StartY=-22.5 StartZ=0 EndX=57.63 EndY=-19.5 EndZ=0
    g74: LineSegment StartX=69.63 StartY=32.9418 StartZ=0 EndX=69.63 EndY=-33.4182 EndZ=0
    g75: LineSegment StartX=-78.3226 StartY=18.5 StartZ=0 EndX=-2.53571 EndY=18.5 EndZ=0
  constraints (221):
    c: Coincident(g0,g1)
    c: Coincident(g1,g2)
    c: Coincident(g2,g3)
    c: Coincident(g3,g0)
    c: Horizontal(g0)
    c: Horizontal(g2)
    c: Vertical(g1)
    c: Vertical(g3)
    c: Distance(g0) = 70
    c: DistanceY(g1,g1) = 12.5
    c: Coincident(g4,g5)
    c: Coincident(g5,g6)
    c: Coincident(g6,g7)
    c: Coincident(g7,g4)
    c: Horizontal(g4)
    c: Horizontal(g6)
    c: Vertical(g5)
    c: Vertical(g7)
    c: Distance(g5) = 28
    c: Distance(g6) = 50
    c: DistanceX(g0) = -75
    c: Distance(g9,g8) = 40
    c: PointOnObject(g10,g7)
    c: Horizontal(g10)
    c: Symmetric(g9,g8,g10)
    c: Symmetric(g4,g5,g10)
    c: Vertical(g11)
    c: PointOnObject(g8,g11)
    c: Diameter(g8) = 2.8
    c: Equal(g8,g9)
    c: DistanceX(g5) = 48
    c: DistanceY(g4) = 5
    c: Coincident(g12,g13)
    c: Coincident(g13,g14)
    c: Coincident(g14,g15)
    c: Coincident(g15,g12)
    c: Horizontal(g12)
    c: Horizontal(g14)
    c: Vertical(g13)
    c: Vertical(g15)
    c: Coincident(g16,g17)
    c: Coincident(g17,g18)
    c: Coincident(g18,g19)
    c: Coincident(g19,g16)
    c: Horizontal(g16)
    c: Horizontal(g18)
    c: Vertical(g17)
    c: Vertical(g19)
    c: Coincident(g20,g21)
    c: Coincident(g21,g22)
    c: Coincident(g22,g23)
    c: Coincident(g23,g20)
    c: Horizontal(g20)
    c: Horizontal(g22)
    c: Vertical(g21)
    c: Vertical(g23)
    c: Distance(g13) = 3
    c: Distance(g17) = 3
    c: Distance(g21) = 3
    c: DistanceY(g12) = 28
    c: DistanceY(g16) = 28
    c: DistanceY(g20) = 28
    c: Distance(g12,g16) = 5
    c: Distance(g16,g20) = 5
    c: Distance(g12) = 12
    c: Coincident(g24,g25)
    c: Coincident(g25,g26)
    c: Coincident(g26,g27)
    c: Coincident(g27,g24)
    c: Horizontal(g24)
    c: Horizontal(g26)
    c: Vertical(g25)
    c: Vertical(g27)
    c: Coincident(g28,g29)
    c: Coincident(g29,g30)
    c: Coincident(g30,g31)
    c: Coincident(g31,g28)
    c: Horizontal(g28)
    c: Horizontal(g30)
    c: Vertical(g29)
    c: Vertical(g31)
    c: Coincident(g32,g33)
    c: Coincident(g33,g34)
    c: Coincident(g34,g35)
    c: Coincident(g35,g32)
    c: Horizontal(g32)
    c: Horizontal(g34)
    c: Vertical(g33)
    c: Vertical(g35)
    c: Distance(g24,g13) = 3
    c: Equal(g27,g15)
    c: Equal(g15,g31)
    c: Equal(g31,g35)
    c: Equal(g14,g24)
    c: Equal(g24,g28)
    c: Equal(g28,g32)
    c: Equal(g32,g22)
    c: Equal(g22,g18)
    c: DistanceX(g13,g24) = 0
    c: Distance(g28,g17) = 3
    c: Distance(g22,g32) = 3
    c: DistanceX(g17,g28) = 0
    c: DistanceX(g22,g32) = 0
    c: Coincident(g38,g36)
    c: Coincident(g38,g37)
    c: Diameter(g36) = 2.8
    c: Equal(g36,g37)
    c: Symmetric(g6,g5,g11)
    c: PointOnObject(g11,g4)
    c: Coincident(g41,g39)
    c: Coincident(g41,g40)
    c: Diameter(g40) = 2.8
    c: Equal(g40,g39)
    c: Distance(g0,g38) = 5
    c: Distance(g0,g41) = 5
    c: Coincident(g42,g43)
    c: Coincident(g43,g44)
    c: Coincident(g44,g45)
    c: Coincident(g45,g42)
    c: Horizontal(g42)
    c: Horizontal(g44)
    c: Vertical(g43)
    c: Vertical(g45)
    c: Coincident(g46,g47)
    c: Coincident(g47,g48)
    c: Coincident(g48,g49)
    c: Coincident(g49,g46)
    c: Horizontal(g46)
    c: Horizontal(g48)
    c: Vertical(g47)
    c: Vertical(g49)
    c: Coincident(g50,g51)
    c: Coincident(g51,g52)
    c: Coincident(g52,g53)
    c: Coincident(g53,g50)
    c: Horizontal(g50)
    c: Horizontal(g52)
    c: Vertical(g51)
    c: Vertical(g53)
    c: Coincident(g54,g55)
    c: Coincident(g55,g56)
    c: Coincident(g56,g57)
    c: Coincident(g57,g54)
    c: Horizontal(g54)
    c: Horizontal(g56)
    c: Vertical(g55)
    c: Vertical(g57)
    c: Coincident(g58,g59)
    c: Coincident(g59,g60)
    c: Coincident(g60,g61)
    c: Coincident(g61,g58)
    c: Horizontal(g58)
    c: Horizontal(g60)
    c: Vertical(g59)
    c: Vertical(g61)
    c: Coincident(g62,g63)
    c: Coincident(g63,g64)
    c: Coincident(g64,g65)
    c: Coincident(g65,g62)
    c: Horizontal(g62)
    c: Horizontal(g64)
    c: Vertical(g63)
    c: Vertical(g65)
    c: Coincident(g66,g67)
    c: Coincident(g67,g68)
    c: Coincident(g68,g69)
    c: Coincident(g69,g66)
    c: Horizontal(g66)
    c: Horizontal(g68)
    c: Vertical(g67)
    c: Vertical(g69)
    c: Coincident(g70,g71)
    c: Coincident(g71,g72)
    c: Coincident(g72,g73)
    c: Coincident(g73,g70)
    c: Horizontal(g70)
    c: Horizontal(g72)
    c: Vertical(g71)
    c: Vertical(g73)
    c: Equal(g71,g67)
    c: Equal(g67,g63)
    c: Equal(g63,g59)
    c: Equal(g59,g55)
    c: Equal(g55,g51)
    c: Equal(g51,g47)
    c: Equal(g47,g43)
    c: Equal(g43,g33)
    c: Equal(g70,g66)
    c: Equal(g66,g62)
    c: Equal(g62,g58)
    c: Equal(g58,g54)
    c: Equal(g54,g50)
    c: Equal(g50,g46)
    c: Equal(g46,g42)
    c: Equal(g42,g22)
    c: Vertical(g74)
    c: PointOnObject(g42,g74)
    c: PointOnObject(g46,g74)
    c: PointOnObject(g50,g74)
    c: PointOnObject(g54,g74)
    c: PointOnObject(g58,g74)
    c: PointOnObject(g62,g74)
    c: PointOnObject(g66,g74)
    c: PointOnObject(g70,g74)
    c: Distance(g44,g46) = 3
    c: Distance(g48,g50) = 3
    c: Distance(g52,g54) = 3
    c: Distance(g56,g58) = 3
    c: Distance(g60,g62) = 3
    c: Distance(g64,g66) = 3
    c: Distance(g68,g70) = 3
    c: DistanceY(g55) = 1.5
    c: DistanceX(g74) = 69.63
    c: Distance(g74) = 66.36
    c: DistanceX(g12) = 3
    c: Symmetric(g2,g0,g75)
    c: Symmetric(g36,g37,g75)
    c: Symmetric(g39,g40,g75)
    c: Distance(g38) = 19
    c: Distance(g41) = 19
    c: DistanceY(g75) = 18.5
FEATURE [Sketcher::SketchObject] Sketch013
  FullyConstrained = true
  MapMode = 5
  Placement = pos=(0,0,4) rot=(0,0,1;0rad)
  Support = -> [Pad006]
  sketch-geometry (21):
    g0: LineSegment StartX=-77.5 StartY=39 StartZ=0 EndX=27.5 EndY=39 EndZ=0
    g1: LineSegment StartX=27.5 StartY=39 StartZ=0 EndX=27.5 EndY=-66 EndZ=0
    g2: LineSegment StartX=27.5 StartY=-66 StartZ=0 EndX=-77.5 EndY=-66 EndZ=0
    g3: LineSegment StartX=-77.5 StartY=-66 StartZ=0 EndX=-77.5 EndY=39 EndZ=0
    g4: Circle CenterX=-25 CenterY=-13.5 CenterZ=0 NormalX=0 NormalY=0 NormalZ=1 AngleXU=0 Radius=55
    g5: Circle CenterX=-77.5 CenterY=39 CenterZ=0 NormalX=0 NormalY=0 NormalZ=1 AngleXU=0 Radius=2.75
    g6: Circle CenterX=27.5 CenterY=39 CenterZ=0 NormalX=0 NormalY=0 NormalZ=1 AngleXU=0 Radius=2.75
    g7: Circle CenterX=27.5 CenterY=-66 CenterZ=0 NormalX=0 NormalY=0 NormalZ=1 AngleXU=0 Radius=2.75
    g8: Circle CenterX=-77.5 CenterY=-66 CenterZ=0 NormalX=0 NormalY=0 NormalZ=1 AngleXU=0 Radius=2.75
    g9: Circle CenterX=-50 CenterY=75 CenterZ=0 NormalX=0 NormalY=0 NormalZ=1 AngleXU=0 Radius=1.75
    g10: Circle CenterX=90 CenterY=-75 CenterZ=0 NormalX=0 NormalY=0 NormalZ=1 AngleXU=0 Radius=1.75
    g11: Circle CenterX=-90 CenterY=-75 CenterZ=0 NormalX=0 NormalY=0 NormalZ=1 AngleXU=0 Radius=1.75
    g12: Circle CenterX=120 CenterY=65 CenterZ=0 NormalX=0 NormalY=0 NormalZ=1 AngleXU=0 Radius=1.75
    g13: Circle CenterX=120 CenterY=-65 CenterZ=0 NormalX=0 NormalY=0 NormalZ=1 AngleXU=0 Radius=1.75
    g14: Circle CenterX=-120 CenterY=65 CenterZ=0 NormalX=0 NormalY=0 NormalZ=1 AngleXU=0 Radius=1.4
    g15: Circle CenterX=-120 CenterY=-65 CenterZ=0 NormalX=0 NormalY=0 NormalZ=1 AngleXU=0 Radius=1.4
    g16: Circle CenterX=100 CenterY=30 CenterZ=0 NormalX=0 NormalY=0 NormalZ=1 AngleXU=0 Radius=1.75
    g17: Circle CenterX=100 CenterY=-30 CenterZ=0 NormalX=0 NormalY=0 NormalZ=1 AngleXU=0 Radius=1.75
    g18: Circle CenterX=50 CenterY=75 CenterZ=0 NormalX=0 NormalY=0 NormalZ=1 AngleXU=0 Radius=1.75
    g19: Circle CenterX=-120 CenterY=0 CenterZ=0 NormalX=0 NormalY=0 NormalZ=1 AngleXU=0 Radius=1.4
    g20: Circle CenterX=120 CenterY=0 CenterZ=0 NormalX=0 NormalY=0 NormalZ=1 AngleXU=0 Radius=1.75
  constraints (53):
    c: Coincident(g0,g1)
    c: Coincident(g1,g2)
    c: Coincident(g2,g3)
    c: Coincident(g3,g0)
    c: Horizontal(g0)
    c: Horizontal(g2)
    c: Vertical(g3)
    c: Distance(g0) = 105
    c: Distance(g1) = 105
    c: Diameter(g4) = 110
    c: DistanceX(g4) = -25
    c: Coincident(g5,g0)
    c: Coincident(g6,g0)
    c: Coincident(g7,g1)
    c: Coincident(g8,g2)
    c: Symmetric(g7,g5,g4)
    c: Equal(g0,g2)
    c: Diameter(g5) = 5.5
    c: Equal(g5,g6)
    c: Equal(g5,g7)
    c: Equal(g5,g8)
    c: Symmetric(g10,g11,g-2)
    c: Distance(g10,g11) = 180
    c: Diameter(g11) = 3.5
    c: Equal(g11,g10)
    c: DistanceY(g10) = -75
    c: Diameter(g9) = 3.5
    c: Diameter(g12) = 3.5
    c: Equal(g12,g13)
    c: Symmetric(g13,g12,g-1)
    c: Distance(g12,g13) = 130
    c: DistanceX(g13) = 120
    c: DistanceX(g14) = -120
    c: Symmetric(g15,g14,g-1)
    c: Distance(g15,g14) = 130
    c: Diameter(g14) = 2.8
    c: Equal(g14,g15)
    c: DistanceY(g4) = -13.5
    c: Diameter(g16) = 3.5
    c: Equal(g16,g17)
    c: Symmetric(g17,g16,g-1)
    c: Distance(g17,g16) = 60
    c: DistanceX(g17) = 100
    c: Symmetric(g18,g9,g-2)
    c: Distance(g9,g18) = 100
    c: DistanceY(g18) = 75
    c: Diameter(g18) = 3.5
    c: PointOnObject(g19,g-1)
    c: Diameter(g19) = 2.8
    c: DistanceX(g19) = -120
    c: PointOnObject(g20,g-1)
    c: Diameter(g20) = 3.5
    c: DistanceX(g20) = 120
FEATURE [PartDesign::Pocket] Pocket005
  BaseFeature = -> Pad006
  Length = 5
  Length2 = 100
  Profile = -> Sketch013
  Type = 0
FEATURE [Sketcher::SketchObject] Sketch014  label="USBholes"
  FullyConstrained = true
  MapMode = 5
  Placement = pos=(0,-3,-7e-16) rot=(1,0,0;1.5708rad)
  Support = -> [Pad003]
  sketch-geometry (8):
    g0: LineSegment StartX=23 StartY=-29 StartZ=0 EndX=23 EndY=-17 EndZ=0
    g1: LineSegment StartX=23 StartY=-17 StartZ=0 EndX=37 EndY=-17 EndZ=0
    g2: LineSegment StartX=37 StartY=-17 StartZ=0 EndX=37 EndY=-29 EndZ=0
    g3: LineSegment StartX=58 StartY=-26 StartZ=0 EndX=58 EndY=-29 EndZ=0
    g4: LineSegment StartX=58 StartY=-26 StartZ=0 EndX=42 EndY=-26 EndZ=0
    g5: LineSegment StartX=23 StartY=-29 StartZ=0 EndX=37 EndY=-29 EndZ=0
    g6: LineSegment StartX=58 StartY=-29 StartZ=0 EndX=42 EndY=-29 EndZ=0
    g7: LineSegment StartX=42 StartY=-26 StartZ=0 EndX=42 EndY=-29 EndZ=0
  constraints (24):
    c: Vertical(g0)
    c: DistanceX(g0) = 23
    c: Coincident(g0,g1)
    c: Horizontal(g1)
    c: Coincident(g1,g2)
    c: Vertical(g2)
    c: Vertical(g3)
    c: Distance(g3) = 3
    c: DistanceY(g3) = -29
    c: Distance(g1) = 14
    c: Distance(g0) = 12
    c: Coincident(g4,g3)
    c: Horizontal(g4)
    c: Distance(g4) = 16
    c: Coincident(g5,g0)
    c: Horizontal(g5)
    c: Coincident(g6,g3)
    c: Horizontal(g6)
    c: Coincident(g7,g4)
    c: Coincident(g7,g6)
    c: Coincident(g5,g2)
    c: DistanceX(g3) = 58
    c: DistanceY(g2) = -29
    c: Vertical(g7)
FEATURE [PartDesign::Pocket] Pocket006
  BaseFeature = -> Pad003
  Length = 5
  Length2 = 100
  Placement = pos=(0,0,0) rot=(1,0,0;1.5708rad)
  Profile = -> Sketch014
  Type = 0
FEATURE [Sketcher::SketchObject] Sketch015
  FullyConstrained = true
  MapMode = 5
  Placement = pos=(0,0,0) rot=(-1,0,0;1.5708rad)
  Support = -> [Pad004]
  sketch-geometry (6):
    g0: Circle CenterX=-113.5 CenterY=15 CenterZ=0 NormalX=0 NormalY=0 NormalZ=1 AngleXU=0 Radius=1.4
    g1: Circle CenterX=113.5 CenterY=-15 CenterZ=0 NormalX=0 NormalY=0 NormalZ=1 AngleXU=0 Radius=1.4
    g2: LineSegment StartX=-115.5 StartY=25 StartZ=0 EndX=115.5 EndY=25 EndZ=0
    g3: LineSegment StartX=115.5 StartY=25 StartZ=0 EndX=115.5 EndY=-25 EndZ=0
    g4: LineSegment StartX=115.5 StartY=-25 StartZ=0 EndX=-115.5 EndY=-25 EndZ=0
    g5: LineSegment StartX=-115.5 StartY=-25 StartZ=0 EndX=-115.5 EndY=25 EndZ=0
  constraints (15):
    c: DistanceY(g1) = -15
    c: DistanceX(g0,g1) = 227
    c: Diameter(g0) = 2.8
    c: Equal(g0,g1)
    c: Coincident(g2,g3)
    c: Coincident(g3,g4)
    c: Coincident(g4,g5)
    c: Coincident(g5,g2)
    c: Horizontal(g4)
    c: Vertical(g5)
    c: Distance(g2) = 231
    c: Symmetric(g2,g2,g-2)
    c: Distance(g3) = 50
    c: Symmetric(g3,g2,g-1)
    c: Symmetric(g1,g0,g-1)
FEATURE [PartDesign::Pocket] Pocket007
  BaseFeature = -> Pad004
  Length = 5
  Length2 = 100
  Placement = pos=(0,0,0) rot=(1,0,0;1.5708rad)
  Profile = -> Sketch015
  Type = 0
FEATURE [Sketcher::SketchObject] Sketch016  label="CenterPad"
  ExternalGeometry = -> [Pocket002]
  FullyConstrained = true
  MapMode = 5
  Placement = pos=(3,-1.3e-15,1.3e-15) rot=(0.57735,0.57735,0.57735;2.0944rad)
  Support = -> [Pocket002]
  sketch-geometry (4):
    g0: LineSegment StartX=-76.5 StartY=31.5 StartZ=0 EndX=76.5 EndY=31.5 EndZ=0
    g1: LineSegment StartX=76.5 StartY=31.5 StartZ=0 EndX=76.5 EndY=-31.5 EndZ=0
    g2: LineSegment StartX=76.5 StartY=-31.5 StartZ=0 EndX=-76.5 EndY=-31.5 EndZ=0
    g3: LineSegment StartX=-76.5 StartY=-31.5 StartZ=0 EndX=-76.5 EndY=31.5 EndZ=0
  constraints (10):
    c: Coincident(g0,g1)
    c: Coincident(g1,g2)
    c: Coincident(g2,g3)
    c: Coincident(g3,g0)
    c: Horizontal(g2)
    c: Vertical(g3)
    c: Distance(g0) = 153
    c: Distance(g1) = 63
    c: Symmetric(g0,g0,g-2)
    c: Symmetric(g1,g0,g-1)
FEATURE [PartDesign::Pad] Pad007
  BaseFeature = -> Pocket002
  Direction = (1,1,1)
  Length = 4
  Length2 = 100
  Placement = pos=(0,0,0) rot=(0.57735,0.57735,0.57735;2.0944rad)
  Profile = -> Sketch016
  Type = 0
FEATURE [PartDesign::Pocket] Pocket008
  BaseFeature = -> Pad007
  Length = 5
  Length2 = 100
  Placement = pos=(0,0,0) rot=(0.57735,0.57735,0.57735;2.0944rad)
  Profile = -> Sketch012
  Type = 1
FEATURE [Sketcher::SketchObject] Sketch021
  FullyConstrained = false
  MapMode = 5
  Placement = pos=(0,0,7) rot=(0,0,1;0rad)
  sketch-geometry (4):
    g0: LineSegment StartX=-5.58191 StartY=14.6169 StartZ=0 EndX=116.05 EndY=14.6169 EndZ=0
    g1: LineSegment StartX=116.05 StartY=14.6169 StartZ=0 EndX=116.05 EndY=-73.9848 EndZ=0
    g2: LineSegment StartX=116.05 StartY=-73.9848 StartZ=0 EndX=-5.58191 EndY=-73.9848 EndZ=0
    g3: LineSegment StartX=-5.58191 StartY=-73.9848 StartZ=0 EndX=-5.58191 EndY=14.6169 EndZ=0
  constraints (8):
    c: Coincident(g0,g1)
    c: Coincident(g1,g2)
    c: Coincident(g2,g3)
    c: Coincident(g3,g0)
    c: Horizontal(g0)
    c: Horizontal(g2)
    c: Vertical(g1)
    c: Vertical(g3)
FEATURE [Sketcher::SketchObject] Sketch019
  FullyConstrained = false
  MapMode = 5
  Placement = pos=(0,0,4) rot=(0,0,1;0rad)
  Support = -> [Pocket]
  sketch-geometry (3):
    g0: Circle CenterX=-110 CenterY=29.3395 CenterZ=0 NormalX=0 NormalY=0 NormalZ=1 AngleXU=0 Radius=1.4
    g1: Circle CenterX=69.6861 CenterY=26.5639 CenterZ=0 NormalX=0 NormalY=0 NormalZ=1 AngleXU=0 Radius=1.4
    g2: Circle CenterX=-68.3728 CenterY=-25.761 CenterZ=0 NormalX=0 NormalY=0 NormalZ=1 AngleXU=0 Radius=1.4
  constraints (4):
    c: Diameter(g0) = 2.8
    c: Equal(g0,g1)
    c: Diameter(g2) = 2.8
    c: DistanceX(g0) = -110
FEATURE [PartDesign::Pocket] Pocket009
  BaseFeature = -> Pocket
  Length = 2
  Length2 = 100
  Profile = -> Sketch019
  Type = 0
FEATURE [Sketcher::SketchObject] Sketch022
  FullyConstrained = false
  MapMode = 5
  Placement = pos=(0,0,4) rot=(0,0,1;0rad)
  Support = -> [Pocket009]
  sketch-geometry (49):
    g0: Circle CenterX=-120 CenterY=65 CenterZ=0 NormalX=0 NormalY=0 NormalZ=1 AngleXU=0 Radius=1.4
    g1: Circle CenterX=-120 CenterY=-65 CenterZ=0 NormalX=0 NormalY=0 NormalZ=1 AngleXU=0 Radius=1.4
    g2: Circle CenterX=120 CenterY=65 CenterZ=0 NormalX=0 NormalY=0 NormalZ=1 AngleXU=0 Radius=1.4
    g3: Circle CenterX=120 CenterY=-65 CenterZ=0 NormalX=0 NormalY=0 NormalZ=1 AngleXU=0 Radius=1.4
    g4: Circle CenterX=-50 CenterY=75 CenterZ=0 NormalX=0 NormalY=0 NormalZ=1 AngleXU=0 Radius=1.75
    g5: Circle CenterX=50 CenterY=75 CenterZ=0 NormalX=0 NormalY=0 NormalZ=1 AngleXU=0 Radius=1.75
    g6: Circle CenterX=-90 CenterY=-75 CenterZ=0 NormalX=0 NormalY=0 NormalZ=1 AngleXU=0 Radius=1.75
    g7: Circle CenterX=-20 CenterY=-75 CenterZ=0 NormalX=0 NormalY=0 NormalZ=1 AngleXU=0 Radius=1.75
    g8: LineSegment StartX=26.7977 StartY=-18.3916 StartZ=0 EndX=41.7977 EndY=-18.3916 EndZ=0
    g9: LineSegment StartX=41.7977 StartY=-18.3916 StartZ=0 EndX=41.7977 EndY=-21.3916 EndZ=0
    g10: LineSegment StartX=41.7977 StartY=-21.3916 StartZ=0 EndX=26.7977 EndY=-21.3916 EndZ=0
    g11: LineSegment StartX=26.7977 StartY=-21.3916 StartZ=0 EndX=26.7977 EndY=-18.3916 EndZ=0
    g12: LineSegment StartX=26.7977 StartY=-31.3916 StartZ=0 EndX=41.7977 EndY=-31.3916 EndZ=0
    g13: LineSegment StartX=41.7977 StartY=-31.3916 StartZ=0 EndX=41.7977 EndY=-34.3916 EndZ=0
    g14: LineSegment StartX=41.7977 StartY=-34.3916 StartZ=0 EndX=26.7977 EndY=-34.3916 EndZ=0
    g15: LineSegment StartX=26.7977 StartY=-34.3916 StartZ=0 EndX=26.7977 EndY=-31.3916 EndZ=0
    g16: LineSegment StartX=26.7977 StartY=-44.3916 StartZ=0 EndX=41.7977 EndY=-44.3916 EndZ=0
    g17: LineSegment StartX=41.7977 StartY=-44.3916 StartZ=0 EndX=41.7977 EndY=-47.3916 EndZ=0
    g18: LineSegment StartX=41.7977 StartY=-47.3916 StartZ=0 EndX=26.7977 EndY=-47.3916 EndZ=0
    g19: LineSegment StartX=26.7977 StartY=-47.3916 StartZ=0 EndX=26.7977 EndY=-44.3916 EndZ=0
    g20: LineSegment StartX=71.7977 StartY=-18.3916 StartZ=0 EndX=86.7977 EndY=-18.3916 EndZ=0
    g21: LineSegment StartX=86.7977 StartY=-18.3916 StartZ=0 EndX=86.7977 EndY=-21.3916 EndZ=0
    g22: LineSegment StartX=86.7977 StartY=-21.3916 StartZ=0 EndX=71.7977 EndY=-21.3916 EndZ=0
    g23: LineSegment StartX=71.7977 StartY=-21.3916 StartZ=0 EndX=71.7977 EndY=-18.3916 EndZ=0
    g24: LineSegment StartX=71.7977 StartY=-31.3916 StartZ=0 EndX=86.7977 EndY=-31.3916 EndZ=0
    g25: LineSegment StartX=86.7977 StartY=-31.3916 StartZ=0 EndX=86.7977 EndY=-34.3916 EndZ=0
    g26: LineSegment StartX=86.7977 StartY=-34.3916 StartZ=0 EndX=71.7977 EndY=-34.3916 EndZ=0
    g27: LineSegment StartX=71.7977 StartY=-34.3916 StartZ=0 EndX=71.7977 EndY=-31.3916 EndZ=0
    g28: LineSegment StartX=71.7977 StartY=-44.3916 StartZ=0 EndX=86.7977 EndY=-44.3916 EndZ=0
    g29: LineSegment StartX=86.7977 StartY=-44.3916 StartZ=0 EndX=86.7977 EndY=-47.3916 EndZ=0
    g30: LineSegment StartX=86.7977 StartY=-47.3916 StartZ=0 EndX=71.7977 EndY=-47.3916 EndZ=0
    g31: LineSegment StartX=71.7977 StartY=-47.3916 StartZ=0 EndX=71.7977 EndY=-44.3916 EndZ=0
    g32: LineSegment StartX=-59.3112 StartY=30.3283 StartZ=0 EndX=-44.3112 EndY=30.3283 EndZ=0
    g33: LineSegment StartX=-44.3112 StartY=30.3283 StartZ=0 EndX=-44.3112 EndY=27.3283 EndZ=0
    g34: LineSegment StartX=-44.3112 StartY=27.3283 StartZ=0 EndX=-59.3112 EndY=27.3283 EndZ=0
    g35: LineSegment StartX=-59.3112 StartY=27.3283 StartZ=0 EndX=-59.3112 EndY=30.3283 EndZ=0
    g36: LineSegment StartX=-59.3112 StartY=22.3283 StartZ=0 EndX=-44.3112 EndY=22.3283 EndZ=0
    g37: LineSegment StartX=-44.3112 StartY=22.3283 StartZ=0 EndX=-44.3112 EndY=19.3283 EndZ=0
    g38: LineSegment StartX=-44.3112 StartY=19.3283 StartZ=0 EndX=-59.3112 EndY=19.3283 EndZ=0
    g39: LineSegment StartX=-59.3112 StartY=19.3283 StartZ=0 EndX=-59.3112 EndY=22.3283 EndZ=0
    g40: LineSegment StartX=-59.3112 StartY=14.3283 StartZ=0 EndX=-44.3112 EndY=14.3283 EndZ=0
    g41: LineSegment StartX=-44.3112 StartY=14.3283 StartZ=0 EndX=-44.3112 EndY=11.3283 EndZ=0
    g42: LineSegment StartX=-44.3112 StartY=11.3283 StartZ=0 EndX=-59.3112 EndY=11.3283 EndZ=0
    g43: LineSegment StartX=-59.3112 StartY=11.3283 StartZ=0 EndX=-59.3112 EndY=14.3283 EndZ=0
    g44: LineSegment StartX=-59.3112 StartY=39.1861 StartZ=0 EndX=-59.3112 EndY=3.92018 EndZ=0
    g45: LineSegment StartX=26.7977 StartY=-8.02324 StartZ=0 EndX=26.7977 EndY=-61.6972 EndZ=0
    g46: LineSegment StartX=71.7977 StartY=-8.28726 StartZ=0 EndX=71.7977 EndY=-63.1239 EndZ=0
    g47: Circle CenterX=-120 CenterY=0 CenterZ=0 NormalX=0 NormalY=0 NormalZ=1 AngleXU=0 Radius=1.4
    g48: Circle CenterX=120 CenterY=0 CenterZ=0 NormalX=0 NormalY=0 NormalZ=1 AngleXU=0 Radius=1.4
  constraints (135):
    c: Symmetric(g3,g1,g-2)
    c: Symmetric(g2,g0,g-2)
    c: Distance(g0,g2) = 240
    c: Diameter(g0) = 2.8
    c: Equal(g0,g1)
    c: Equal(g0,g2)
    c: Equal(g0,g3)
    c: Symmetric(g1,g0,g-1)
    c: Distance(g1,g0) = 130
    c: Diameter(g7) = 3.5
    c: Equal(g7,g6)
    c: DistanceY(g7) = -75
    c: Diameter(g4) = 3.5
    c: Equal(g4,g5)
    c: Symmetric(g5,g4,g-2)
    c: Distance(g5,g4) = 100
    c: DistanceY(g5) = 75
    c: Coincident(g8,g9)
    c: Coincident(g9,g10)
    c: Coincident(g10,g11)
    c: Coincident(g11,g8)
    c: Horizontal(g8)
    c: Horizontal(g10)
    c: Vertical(g9)
    c: Vertical(g11)
    c: Coincident(g12,g13)
    c: Coincident(g13,g14)
    c: Coincident(g14,g15)
    c: Coincident(g15,g12)
    c: Horizontal(g12)
    c: Horizontal(g14)
    c: Vertical(g13)
    c: Vertical(g15)
    c: Coincident(g16,g17)
    c: Coincident(g17,g18)
    c: Coincident(g18,g19)
    c: Coincident(g19,g16)
    c: Horizontal(g16)
    c: Horizontal(g18)
    c: Vertical(g17)
    c: Vertical(g19)
    c: Coincident(g20,g21)
    c: Coincident(g21,g22)
    c: Coincident(g22,g23)
    c: Coincident(g23,g20)
    c: Horizontal(g20)
    c: Horizontal(g22)
    c: Vertical(g21)
    c: Vertical(g23)
    c: Coincident(g24,g25)
    c: Coincident(g25,g26)
    c: Coincident(g26,g27)
    c: Coincident(g27,g24)
    c: Horizontal(g24)
    c: Horizontal(g26)
    c: Vertical(g25)
    c: Vertical(g27)
    c: Coincident(g28,g29)
    c: Coincident(g29,g30)
    c: Coincident(g30,g31)
    c: Coincident(g31,g28)
    c: Horizontal(g28)
    c: Horizontal(g30)
    c: Vertical(g29)
    c: Vertical(g31)
    c: Coincident(g32,g33)
    c: Coincident(g33,g34)
    c: Coincident(g34,g35)
    c: Coincident(g35,g32)
    c: Horizontal(g32)
    c: Horizontal(g34)
    c: Vertical(g33)
    c: Vertical(g35)
    c: Coincident(g36,g37)
    c: Coincident(g37,g38)
    c: Coincident(g38,g39)
    c: Coincident(g39,g36)
    c: Horizontal(g36)
    c: Horizontal(g38)
    c: Vertical(g37)
    c: Vertical(g39)
    c: Coincident(g40,g41)
    c: Coincident(g41,g42)
    c: Coincident(g42,g43)
    c: Coincident(g43,g40)
    c: Horizontal(g40)
    c: Horizontal(g42)
    c: Vertical(g41)
    c: Vertical(g43)
    c: Vertical(g44)
    c: Vertical(g45)
    c: Vertical(g46)
    c: PointOnObject(g32,g44)
    c: PointOnObject(g36,g44)
    c: PointOnObject(g40,g44)
    c: PointOnObject(g8,g45)
    c: PointOnObject(g12,g45)
    c: PointOnObject(g16,g45)
    c: PointOnObject(g20,g46)
    c: PointOnObject(g24,g46)
    c: PointOnObject(g28,g46)
    c: Equal(g9,g13)
    c: Equal(g13,g17)
    c: Equal(g17,g29)
    c: Equal(g29,g25)
    c: Equal(g25,g21)
    c: Equal(g21,g41)
    c: Equal(g41,g37)
    c: Equal(g37,g33)
    c: Distance(g33) = 3
    c: Equal(g16,g14)
    c: Equal(g14,g26)
    c: Equal(g26,g28)
    c: Equal(g28,g22)
    c: Equal(g22,g8)
    c: Equal(g8,g40)
    c: Equal(g40,g38)
    c: Equal(g38,g34)
    c: Distance(g34) = 15
    c: Distance(g36,g34) = 5
    c: Distance(g38,g40) = 5
    c: Distance(g16,g14) = 10
    c: Distance(g12,g10) = 10
    c: Distance(g24,g22) = 10
    c: Distance(g26,g28) = 10
    c: DistanceY(g8,g20) = 0
    c: Distance(g9,g22) = 30
    c: DistanceY(g6) = -75
    c: DistanceX(g7) = -20
    c: DistanceX(g6) = -90
    c: PointOnObject(g47,g-1)
    c: Diameter(g47) = 2.8
    c: Symmetric(g48,g47,g-1)
    c: Diameter(g48) = 2.8
    c: Distance(g48,g47) = 240
FEATURE [PartDesign::Pocket] Pocket010
  BaseFeature = -> Pocket009
  Length = 5
  Length2 = 100
  Profile = -> Sketch022
  Type = 0
FEATURE [Sketcher::SketchObject] Sketch023  label="AllScrewHoles"
  FullyConstrained = true
  MapMode = 5
  Placement = pos=(-1.12e-14,1.76e-14,40) rot=(0,0,-1;1.5708rad)
  Support = -> [Pocket008]
  sketch-geometry (3):
    g0: Circle CenterX=-65 CenterY=8.5 CenterZ=0 NormalX=0 NormalY=0 NormalZ=1 AngleXU=0 Radius=1.75
    g1: Circle CenterX=65 CenterY=8.5 CenterZ=0 NormalX=0 NormalY=0 NormalZ=1 AngleXU=0 Radius=1.75
    g2: Circle CenterX=0 CenterY=8.5 CenterZ=0 NormalX=0 NormalY=0 NormalZ=1 AngleXU=0 Radius=1.75
  constraints (8):
    c: DistanceY(g0) = 8.5
    c: Symmetric(g1,g0,g-2)
    c: Distance(g0,g1) = 130
    c: Diameter(g0) = 3.5
    c: Diameter(g1) = 3.5
    c: DistanceY(g2) = 8.5
    c: Diameter(g2) = 3.5
    c: PointOnObject(g2,g-2)
FEATURE [PartDesign::Pocket] Pocket011
  BaseFeature = -> Pocket008
  Length = 5
  Length2 = 100
  Placement = pos=(0,0,0) rot=(0.57735,0.57735,0.57735;2.0944rad)
  Profile = -> Sketch023
  Type = 1
FEATURE [Sketcher::SketchObject] Sketch024  label="AccessNotch"
  FullyConstrained = false
  MapMode = 5
  Placement = pos=(-1.12e-14,1.76e-14,40) rot=(0,0,-1;1.5708rad)
  Support = -> [MultiTransform]
  sketch-geometry (4):
    g0: LineSegment StartX=-80.25 StartY=9 StartZ=0 EndX=80.25 EndY=9 EndZ=0
    g1: LineSegment StartX=80.25 StartY=9 StartZ=0 EndX=80.25 EndY=-7.04103 EndZ=0
    g2: LineSegment StartX=80.25 StartY=-7.04103 StartZ=0 EndX=-80.25 EndY=-7.04103 EndZ=0
    g3: LineSegment StartX=-80.25 StartY=-7.04103 StartZ=0 EndX=-80.25 EndY=9 EndZ=0
  constraints (10):
    c: Coincident(g0,g1)
    c: Coincident(g1,g2)
    c: Coincident(g2,g3)
    c: Coincident(g3,g0)
    c: Horizontal(g0)
    c: Vertical(g1)
    c: Vertical(g3)
    c: Symmetric(g1,g2,g-2)
    c: DistanceY(g0) = 9
    c: Distance(g2) = 160.5
FEATURE [PartDesign::Pocket] Pocket012
  BaseFeature = -> MultiTransform
  Length = 5
  Length2 = 100
  Placement = pos=(0,0,0) rot=(0.57735,0.57735,0.57735;2.0944rad)
  Profile = -> Sketch024
  Type = 0
FEATURE [Sketcher::SketchObject] Sketch025  label="2.8mmHoles"
  FullyConstrained = true
  MapMode = 5
  Placement = pos=(-1.12e-14,1.76e-14,40) rot=(0,0,-1;1.5708rad)
  Support = -> [Pocket012]
  sketch-geometry (3):
    g0: Circle CenterX=-65 CenterY=3.5 CenterZ=0 NormalX=0 NormalY=0 NormalZ=1 AngleXU=0 Radius=1.4
    g1: Circle CenterX=65 CenterY=3.5 CenterZ=0 NormalX=0 NormalY=0 NormalZ=1 AngleXU=0 Radius=1.4
    g2: Circle CenterX=0 CenterY=3.5 CenterZ=0 NormalX=0 NormalY=0 NormalZ=1 AngleXU=0 Radius=1.4
  constraints (8):
    c: DistanceY(g1) = 3.5
    c: Symmetric(g0,g1,g-2)
    c: Distance(g1,g0) = 130
    c: Diameter(g1) = 2.8
    c: Equal(g1,g0)
    c: PointOnObject(g2,g-2)
    c: DistanceY(g2) = 3.5
    c: Diameter(g2) = 2.8
FEATURE [Sketcher::SketchObject] Sketch026  label="3.5mmholes"
  FullyConstrained = true
  MapMode = 5
  Placement = pos=(6.9e-14,-4e-14,-40) rot=(0.707107,0.707107,0;3.14159rad)
  sketch-geometry (3):
    g0: Circle CenterX=-65 CenterY=3.5 CenterZ=0 NormalX=0 NormalY=0 NormalZ=1 AngleXU=0 Radius=1.75
    g1: Circle CenterX=65 CenterY=3.5 CenterZ=0 NormalX=0 NormalY=0 NormalZ=1 AngleXU=0 Radius=1.75
    g2: Circle CenterX=0 CenterY=3.5 CenterZ=0 NormalX=0 NormalY=0 NormalZ=1 AngleXU=0 Radius=1.75
  constraints (8):
    c: Diameter(g1) = 3.5
    c: Equal(g1,g0)
    c: Distance(g1,g0) = 130
    c: Symmetric(g1,g0,g-2)
    c: DistanceY(g1) = 3.5
    c: PointOnObject(g2,g-2)
    c: Diameter(g2) = 3.5
    c: DistanceY(g2) = 3.5
FEATURE [Sketcher::SketchObject] Sketch029  label="pads1"
  FullyConstrained = true
  MapMode = 5
  Placement = pos=(0,0,32.5) rot=(0,0,1;3.14159rad)
  Support = -> [Pocket006]
  sketch-geometry (8):
    g0: LineSegment StartX=-85 StartY=1 StartZ=0 EndX=-95 EndY=1 EndZ=0
    g1: LineSegment StartX=-95 StartY=1 StartZ=0 EndX=-95 EndY=-7 EndZ=0
    g2: LineSegment StartX=-95 StartY=-7 StartZ=0 EndX=-85 EndY=-7 EndZ=0
    g3: LineSegment StartX=-85 StartY=-7 StartZ=0 EndX=-85 EndY=1 EndZ=0
    g4: LineSegment StartX=85 StartY=1 StartZ=0 EndX=95 EndY=1 EndZ=0
    g5: LineSegment StartX=95 StartY=1 StartZ=0 EndX=95 EndY=-7 EndZ=0
    g6: LineSegment StartX=95 StartY=-7 StartZ=0 EndX=85 EndY=-7 EndZ=0
    g7: LineSegment StartX=85 StartY=-7 StartZ=0 EndX=85 EndY=1 EndZ=0
  constraints (23):
    c: Coincident(g0,g1)
    c: Coincident(g1,g2)
    c: Coincident(g2,g3)
    c: Coincident(g3,g0)
    c: Horizontal(g0)
    c: Horizontal(g2)
    c: Vertical(g1)
    c: Vertical(g3)
    c: Coincident(g4,g5)
    c: Coincident(g5,g6)
    c: Coincident(g6,g7)
    c: Coincident(g7,g4)
    c: Horizontal(g4)
    c: Horizontal(g6)
    c: Vertical(g5)
    c: Vertical(g7)
    c: Distance(g4) = 10
    c: Distance(g0) = 10
    c: Distance(g1) = 8
    c: Distance(g5) = 8
    c: DistanceY(g4) = 1
    c: DistanceX(g1) = -95
    c: Symmetric(g5,g1,g-2)
FEATURE [PartDesign::Pad] Pad010
  BaseFeature = -> Pocket006
  Direction = (1,1,1)
  Length = 10
  Length2 = 100
  Placement = pos=(0,0,0) rot=(1,0,0;1.5708rad)
  Profile = -> Sketch029
  Reversed = true
  Type = 0
FEATURE [Sketcher::SketchObject] Sketch030  label="ScrewHoles1"
  FullyConstrained = true
  MapMode = 5
  Placement = pos=(0,-5.8e-14,-32.5) rot=(1,0,0;3.14159rad)
  sketch-geometry (2):
    g0: Circle CenterX=-20 CenterY=-2 CenterZ=0 NormalX=0 NormalY=0 NormalZ=1 AngleXU=0 Radius=1.4
    g1: Circle CenterX=-90 CenterY=-2 CenterZ=0 NormalX=0 NormalY=0 NormalZ=1 AngleXU=0 Radius=1.4
  constraints (6):
    c: Diameter(g0) = 2.8
    c: DistanceX(g0) = -20
    c: Diameter(g1) = 2.8
    c: DistanceY(g1) = -2
    c: DistanceY(g0) = -2
    c: DistanceX(g1) = -90
FEATURE [Sketcher::SketchObject] Sketch032
  FullyConstrained = true
  MapMode = 5
  Placement = pos=(0,0,32.5) rot=(0,0,1;3.14159rad)
  Support = -> [Pocket007]
  sketch-geometry (8):
    g0: LineSegment StartX=-55 StartY=9 StartZ=0 EndX=-45 EndY=9 EndZ=0
    g1: LineSegment StartX=-45 StartY=9 StartZ=0 EndX=-45 EndY=1 EndZ=0
    g2: LineSegment StartX=-45 StartY=1 StartZ=0 EndX=-55 EndY=1 EndZ=0
    g3: LineSegment StartX=-55 StartY=1 StartZ=0 EndX=-55 EndY=9 EndZ=0
    g4: LineSegment StartX=45 StartY=9 StartZ=0 EndX=55 EndY=9 EndZ=0
    g5: LineSegment StartX=55 StartY=9 StartZ=0 EndX=55 EndY=1 EndZ=0
    g6: LineSegment StartX=55 StartY=1 StartZ=0 EndX=45 EndY=1 EndZ=0
    g7: LineSegment StartX=45 StartY=1 StartZ=0 EndX=45 EndY=9 EndZ=0
  constraints (23):
    c: Coincident(g0,g1)
    c: Coincident(g1,g2)
    c: Coincident(g2,g3)
    c: Coincident(g3,g0)
    c: Horizontal(g0)
    c: Horizontal(g2)
    c: Vertical(g1)
    c: Vertical(g3)
    c: Coincident(g4,g5)
    c: Coincident(g5,g6)
    c: Coincident(g6,g7)
    c: Coincident(g7,g4)
    c: Horizontal(g4)
    c: Horizontal(g6)
    c: Vertical(g5)
    c: Vertical(g7)
    c: Symmetric(g5,g2,g-2)
    c: DistanceX(g5) = 55
    c: Equal(g2,g6)
    c: Distance(g2) = 10
    c: DistanceY(g5) = 1
    c: Distance(g1) = 8
    c: Equal(g7,g1)
FEATURE [PartDesign::Pad] Pad011
  BaseFeature = -> Pocket007
  Direction = (1,1,1)
  Length = 6
  Length2 = 100
  Placement = pos=(0,0,0) rot=(1,0,0;1.5708rad)
  Profile = -> Sketch032
  Reversed = true
  Type = 0
FEATURE [PartDesign::Mirrored] Mirrored
  BaseFeature = -> Pad011
  MirrorPlane = -> XY_Plane003
  Originals = -> [Pad011]
  Placement = pos=(0,0,0) rot=(1,0,0;1.5708rad)
FEATURE [Sketcher::SketchObject] Sketch033
  FullyConstrained = false
  MapMode = 5
  Placement = pos=(0,0,32.5) rot=(0,0,1;3.14159rad)
  Support = -> [Mirrored]
  sketch-geometry (2):
    g0: Circle CenterX=-50 CenterY=5 CenterZ=0 NormalX=0 NormalY=0 NormalZ=1 AngleXU=0 Radius=1.2282
    g1: Circle CenterX=50 CenterY=5 CenterZ=0 NormalX=0 NormalY=0 NormalZ=1 AngleXU=0 Radius=1.08034
  constraints (3):
    c: DistanceY(g1) = 5
    c: Symmetric(g0,g1,g-2)
    c: Distance(g1,g0) = 100
FEATURE [PartDesign::Pocket] Pocket017
  BaseFeature = -> Mirrored
  Length = 5
  Length2 = 100
  Placement = pos=(0,0,0) rot=(1,0,0;1.5708rad)
  Profile = -> Sketch033
  Type = 1
FEATURE [Sketcher::SketchObject] Sketch034  label="pads2"
  FullyConstrained = true
  MapMode = 5
  Placement = pos=(-1e-15,-6.5e-14,-32.5) rot=(1,0,0;3.14159rad)
  sketch-geometry (8):
    g0: LineSegment StartX=-15 StartY=1 StartZ=0 EndX=-25 EndY=1 EndZ=0
    g1: LineSegment StartX=-25 StartY=1 StartZ=0 EndX=-25 EndY=-7 EndZ=0
    g2: LineSegment StartX=-25 StartY=-7 StartZ=0 EndX=-15 EndY=-7 EndZ=0
    g3: LineSegment StartX=-15 StartY=-7 StartZ=0 EndX=-15 EndY=1 EndZ=0
    g4: LineSegment StartX=-95 StartY=1 StartZ=0 EndX=-85 EndY=1 EndZ=0
    g5: LineSegment StartX=-85 StartY=1 StartZ=0 EndX=-85 EndY=-7 EndZ=0
    g6: LineSegment StartX=-85 StartY=-7 StartZ=0 EndX=-95 EndY=-7 EndZ=0
    g7: LineSegment StartX=-95 StartY=-7 StartZ=0 EndX=-95 EndY=1 EndZ=0
  constraints (24):
    c: Coincident(g0,g1)
    c: Coincident(g1,g2)
    c: Coincident(g2,g3)
    c: Coincident(g3,g0)
    c: Horizontal(g0)
    c: Horizontal(g2)
    c: Vertical(g1)
    c: Vertical(g3)
    c: DistanceX(g1) = -25
    c: Distance(g2) = 10
    c: Distance(g3) = 8
    c: DistanceY(g2) = -7
    c: Coincident(g4,g5)
    c: Coincident(g5,g6)
    c: Coincident(g6,g7)
    c: Coincident(g7,g4)
    c: Horizontal(g4)
    c: Horizontal(g6)
    c: Vertical(g5)
    c: Vertical(g7)
    c: Distance(g6) = 10
    c: DistanceY(g4) = 1
    c: Distance(g5) = 8
    c: DistanceX(g6) = -95
FEATURE [PartDesign::Pad] Pad012
  BaseFeature = -> Pad010
  Direction = (1,1,1)
  Length = 10
  Length2 = 100
  Placement = pos=(0,0,0) rot=(1,0,0;1.5708rad)
  Profile = -> Sketch034
  Reversed = true
  Type = 0
FEATURE [Sketcher::SketchObject] Sketch036
  FullyConstrained = false
  MapMode = 5
  Placement = pos=(0,-3,-7e-16) rot=(1,0,0;1.5708rad)
  Support = -> [Pocket017]
  sketch-geometry (13):
    g0: Circle CenterX=-113.497 CenterY=-14.9967 CenterZ=0 NormalX=0 NormalY=0 NormalZ=1 AngleXU=0 Radius=1.4
    g1: Circle CenterX=-113.497 CenterY=-14.9967 CenterZ=0 NormalX=0 NormalY=0 NormalZ=1 AngleXU=0 Radius=5
    g2: Circle CenterX=113.51 CenterY=14.9669 CenterZ=0 NormalX=0 NormalY=0 NormalZ=1 AngleXU=0 Radius=1.4
    g3: Circle CenterX=113.51 CenterY=14.9669 CenterZ=0 NormalX=0 NormalY=0 NormalZ=1 AngleXU=0 Radius=5
    g4: Circle CenterX=0 CenterY=0 CenterZ=0 NormalX=0 NormalY=0 NormalZ=1 AngleXU=0 Radius=5.45626
    g5: LineSegment StartX=-105.368 StartY=16 StartZ=0 EndX=104.632 EndY=16 EndZ=0
    g6: LineSegment StartX=104.632 StartY=16 StartZ=0 EndX=104.632 EndY=12 EndZ=0
    g7: LineSegment StartX=104.632 StartY=12 StartZ=0 EndX=-105.368 EndY=12 EndZ=0
    g8: LineSegment StartX=-105.368 StartY=12 StartZ=0 EndX=-105.368 EndY=16 EndZ=0
    g9: LineSegment StartX=-104.632 StartY=-12 StartZ=0 EndX=105.368 EndY=-12 EndZ=0
    g10: LineSegment StartX=105.368 StartY=-12 StartZ=0 EndX=105.368 EndY=-16 EndZ=0
    g11: LineSegment StartX=105.368 StartY=-16 StartZ=0 EndX=-104.632 EndY=-16 EndZ=0
    g12: LineSegment StartX=-104.632 StartY=-16 StartZ=0 EndX=-104.632 EndY=-12 EndZ=0
  constraints (29):
    c: Coincident(g1,g0)
    c: Coincident(g3,g2)
    c: Diameter(g0) = 2.8
    c: Diameter(g1) = 10
    c: Diameter(g2) = 2.8
    c: Diameter(g3) = 10
    c: Coincident(g4,g-1)
    c: Coincident(g5,g6)
    c: Coincident(g6,g7)
    c: Coincident(g7,g8)
    c: Coincident(g8,g5)
    c: Horizontal(g5)
    c: Horizontal(g7)
    c: Vertical(g6)
    c: Vertical(g8)
    c: Coincident(g9,g10)
    c: Coincident(g10,g11)
    c: Coincident(g11,g12)
    c: Coincident(g12,g9)
    c: Horizontal(g9)
    c: Horizontal(g11)
    c: Vertical(g10)
    c: Vertical(g12)
    c: Distance(g12) = 4
    c: Distance(g8) = 4
    c: Distance(g5) = 210
    c: Distance(g9) = 210
    c: Symmetric(g9,g7,g4)
    c: DistanceY(g6) = 12
FEATURE [PartDesign::Pad] Pad013
  BaseFeature = -> Pocket017
  Direction = (1,1,1)
  Length = 2
  Length2 = 100
  Placement = pos=(0,0,0) rot=(1,0,0;1.5708rad)
  Profile = -> Sketch036
  Type = 0
FEATURE [Sketcher::SketchObject] Sketch037
  FullyConstrained = false
  MapMode = 5
  Placement = pos=(0,-3,-7e-16) rot=(1,0,0;1.5708rad)
  Support = -> [Pad013]
  sketch-geometry (4):
    g0: LineSegment StartX=-85 StartY=1.30623 StartZ=0 EndX=-100 EndY=1.30623 EndZ=0
    g1: LineSegment StartX=-100 StartY=1.30623 StartZ=0 EndX=-100 EndY=-1.69377 EndZ=0
    g2: LineSegment StartX=-100 StartY=-1.69377 StartZ=0 EndX=-85 EndY=-1.69377 EndZ=0
    g3: LineSegment StartX=-85 StartY=-1.69377 StartZ=0 EndX=-85 EndY=1.30623 EndZ=0
  constraints (11):
    c: Coincident(g0,g1)
    c: Coincident(g1,g2)
    c: Coincident(g2,g3)
    c: Coincident(g3,g0)
    c: Horizontal(g0)
    c: Horizontal(g2)
    c: Vertical(g1)
    c: Vertical(g3)
    c: Distance(g0) = 15
    c: Distance(g1) = 3
    c: DistanceX(g0) = -100
FEATURE [PartDesign::Pocket] Pocket019
  BaseFeature = -> Pad013
  Length = 5
  Length2 = 100
  Placement = pos=(0,0,0) rot=(1,0,0;1.5708rad)
  Profile = -> Sketch037
  Type = 0
FEATURE [PartDesign::LinearPattern] LinearPattern002
  Direction = -> Sketch037 [H_Axis]
  Length = 184
  Occurrences = 6
  Placement = pos=(0,0,0) rot=(1,0,0;1.5708rad)
FEATURE [PartDesign::MultiTransform] MultiTransform001
  BaseFeature = -> Pocket019
  Originals = -> [Pocket019]
  Placement = pos=(0,0,0) rot=(1,0,0;1.5708rad)
  Transformations = -> [LinearPattern002]
FEATURE [Sketcher::SketchObject] Sketch038  label="ScrewHoles2"
  FullyConstrained = false
  MapMode = 5
  Placement = pos=(0,0,32.5) rot=(0,0,1;3.14159rad)
  Support = -> [Pad012]
  sketch-geometry (2):
    g0: Circle CenterX=-90 CenterY=-2 CenterZ=0 NormalX=0 NormalY=0 NormalZ=1 AngleXU=0 Radius=1.49666
    g1: Circle CenterX=90 CenterY=-2 CenterZ=0 NormalX=0 NormalY=0 NormalZ=1 AngleXU=0 Radius=1.36472
  constraints (3):
    c: Symmetric(g1,g0,g-2)
    c: DistanceX(g0) = -90
    c: DistanceY(g0) = -2
FEATURE [Sketcher::SketchObject] Sketch039  label="psuClearance"
  FullyConstrained = true
  MapMode = 5
  Placement = pos=(7,-9e-15,6e-15) rot=(0.57735,0.57735,0.57735;2.0944rad)
  sketch-geometry (4):
    g0: LineSegment StartX=44 StartY=26 StartZ=0 EndX=76 EndY=26 EndZ=0
    g1: LineSegment StartX=76 StartY=26 StartZ=0 EndX=76 EndY=-26 EndZ=0
    g2: LineSegment StartX=76 StartY=-26 StartZ=0 EndX=44 EndY=-26 EndZ=0
    g3: LineSegment StartX=44 StartY=-26 StartZ=0 EndX=44 EndY=26 EndZ=0
  constraints (11):
    c: Coincident(g0,g1)
    c: Coincident(g1,g2)
    c: Coincident(g2,g3)
    c: Coincident(g3,g0)
    c: Horizontal(g0)
    c: Horizontal(g2)
    c: Vertical(g3)
    c: Distance(g1) = 52
    c: Symmetric(g1,g0,g-1)
    c: Distance(g2) = 32
    c: DistanceX(g1) = 76
FEATURE [Sketcher::SketchObject] Sketch040  label="PsuClearance"
  FullyConstrained = true
  MapMode = 5
  Placement = pos=(0,0,0) rot=(0.57735,0.57735,-0.57735;4.18879rad)
  sketch-geometry (4):
    g0: LineSegment StartX=43 StartY=26 StartZ=0 EndX=75 EndY=26 EndZ=0
    g1: LineSegment StartX=75 StartY=26 StartZ=0 EndX=75 EndY=-26 EndZ=0
    g2: LineSegment StartX=75 StartY=-26 StartZ=0 EndX=43 EndY=-26 EndZ=0
    g3: LineSegment StartX=43 StartY=-26 StartZ=0 EndX=43 EndY=26 EndZ=0
  constraints (11):
    c: Coincident(g0,g1)
    c: Coincident(g1,g2)
    c: Coincident(g2,g3)
    c: Coincident(g3,g0)
    c: Horizontal(g0)
    c: Horizontal(g2)
    c: Vertical(g3)
    c: Distance(g0) = 32
    c: Distance(g1) = 52
    c: Symmetric(g1,g0,g-1)
    c: DistanceX(g1) = 75
FEATURE [Sketcher::SketchObject] Sketch041  label="stiffener"
  FullyConstrained = false
  MapMode = 5
  Placement = pos=(0,0,0) rot=(-1,0,0;1.5708rad)
  sketch-geometry (4):
    g0: LineSegment StartX=-105 StartY=2.5 StartZ=0 EndX=105 EndY=2.5 EndZ=0
    g1: LineSegment StartX=105 StartY=2.5 StartZ=0 EndX=105 EndY=-1.5 EndZ=0
    g2: LineSegment StartX=105 StartY=-1.5 StartZ=0 EndX=-105 EndY=-1.5 EndZ=0
    g3: LineSegment StartX=-105 StartY=-1.5 StartZ=0 EndX=-105 EndY=2.5 EndZ=0
  constraints (10):
    c: Coincident(g0,g1)
    c: Coincident(g1,g2)
    c: Coincident(g2,g3)
    c: Coincident(g3,g0)
    c: Horizontal(g0)
    c: Vertical(g1)
    c: Vertical(g3)
    c: Distance(g3) = 4
    c: Distance(g0) = 210
    c: Symmetric(g1,g2,g-2)
FEATURE [Sketcher::SketchObject] Sketch042  label="cornerPad"
  FullyConstrained = true
  MapMode = 5
  Placement = pos=(-125,0,0) rot=(0.707107,0,-0.707107;3.14159rad)
  sketch-geometry (4):
    g0: LineSegment StartX=32.5 StartY=3 StartZ=0 EndX=34.5 EndY=3 EndZ=0
    g1: LineSegment StartX=34.5 StartY=3 StartZ=0 EndX=34.5 EndY=1 EndZ=0
    g2: LineSegment StartX=34.5 StartY=1 StartZ=0 EndX=32.5 EndY=1 EndZ=0
    g3: LineSegment StartX=32.5 StartY=3 StartZ=0 EndX=32.5 EndY=1 EndZ=0
  constraints (12):
    c: Horizontal(g0)
    c: Coincident(g1,g0)
    c: Coincident(g2,g1)
    c: Coincident(g3,g0)
    c: Coincident(g3,g2)
    c: Vertical(g3)
    c: Distance(g0) = 2
    c: Distance(g1) = 2
    c: Vertical(g1)
    c: Equal(g3,g1)
    c: DistanceY(g0) = 3
    c: DistanceX(g0) = 32.5
FEATURE [Sketcher::SketchObject] Sketch043
  FullyConstrained = true
  MapMode = 5
  Placement = pos=(-125,0,0) rot=(0.57735,-0.57735,-0.57735;2.0944rad)
  Support = -> [Pocket010]
  sketch-geometry (8):
    g0: LineSegment StartX=80 StartY=4 StartZ=0 EndX=78 EndY=4 EndZ=0
    g1: LineSegment StartX=78 StartY=4 StartZ=0 EndX=78 EndY=2 EndZ=0
    g2: LineSegment StartX=78 StartY=2 StartZ=0 EndX=80 EndY=2 EndZ=0
    g3: LineSegment StartX=80 StartY=2 StartZ=0 EndX=80 EndY=4 EndZ=0
    g4: LineSegment StartX=-80 StartY=4 StartZ=0 EndX=-78 EndY=4 EndZ=0
    g5: LineSegment StartX=-78 StartY=4 StartZ=0 EndX=-78 EndY=2 EndZ=0
    g6: LineSegment StartX=-78 StartY=2 StartZ=0 EndX=-80 EndY=2 EndZ=0
    g7: LineSegment StartX=-80 StartY=2 StartZ=0 EndX=-80 EndY=4 EndZ=0
  constraints (24):
    c: Coincident(g0,g1)
    c: Coincident(g1,g2)
    c: Coincident(g2,g3)
    c: Coincident(g3,g0)
    c: Horizontal(g0)
    c: Horizontal(g2)
    c: Vertical(g1)
    c: Vertical(g3)
    c: Distance(g2) = 2
    c: Distance(g1) = 2
    c: DistanceY(g0) = 4
    c: DistanceX(g0) = 80
    c: Coincident(g4,g5)
    c: Coincident(g5,g6)
    c: Coincident(g6,g7)
    c: Coincident(g7,g4)
    c: Horizontal(g4)
    c: Horizontal(g6)
    c: Vertical(g5)
    c: Vertical(g7)
    c: Distance(g7) = 2
    c: Distance(g4) = 2
    c: DistanceY(g4) = 4
    c: DistanceX(g4) = -80
FEATURE [PartDesign::Pocket] Pocket025
  BaseFeature = -> Pocket010
  Length = 5
  Length2 = 100
  Profile = -> Sketch043
  Type = 1
FEATURE [Sketcher::SketchObject] Sketch044
  FullyConstrained = true
  MapMode = 5
  Placement = pos=(-125,0,0) rot=(0.707107,0,-0.707107;3.14159rad)
  Support = -> [MultiTransform001]
  sketch-geometry (4):
    g0: LineSegment StartX=-32.5 StartY=0 StartZ=0 EndX=-34.5 EndY=0 EndZ=0
    g1: LineSegment StartX=-34.5 StartY=0 StartZ=0 EndX=-34.5 EndY=2 EndZ=0
    g2: LineSegment StartX=-34.5 StartY=2 StartZ=0 EndX=-32.5 EndY=2 EndZ=0
    g3: LineSegment StartX=-32.5 StartY=2 StartZ=0 EndX=-32.5 EndY=0 EndZ=0
  constraints (12):
    c: Coincident(g0,g1)
    c: Coincident(g1,g2)
    c: Coincident(g2,g3)
    c: Coincident(g3,g0)
    c: Horizontal(g0)
    c: Horizontal(g2)
    c: Vertical(g1)
    c: Vertical(g3)
    c: PointOnObject(g0,g-1)
    c: Distance(g2) = 2
    c: Distance(g1) = 2
    c: DistanceX(g0) = -32.5
FEATURE [PartDesign::Pad] Pad017
  BaseFeature = -> MultiTransform001
  Direction = (1,1,1)
  Length = 250
  Length2 = 100
  Placement = pos=(0,0,0) rot=(1,0,0;1.5708rad)
  Profile = -> Sketch044
  Reversed = true
  Type = 0
FEATURE [Sketcher::SketchObject] Sketch045
  FullyConstrained = false
  MapMode = 5
  Support = -> [XY_Plane006]
  sketch-geometry (5):
    g0: LineSegment StartX=95 StartY=40 StartZ=0 EndX=105 EndY=40 EndZ=0
    g1: LineSegment StartX=105 StartY=40 StartZ=0 EndX=105 EndY=-40 EndZ=0
    g2: LineSegment StartX=105 StartY=-40 StartZ=0 EndX=95 EndY=-40 EndZ=0
    g3: LineSegment StartX=95 StartY=-40 StartZ=0 EndX=95 EndY=40 EndZ=0
    g4: LineSegment StartX=100 StartY=48.1766 StartZ=0 EndX=100 EndY=-54.3011 EndZ=0
  constraints (12):
    c: Coincident(g0,g1)
    c: Coincident(g1,g2)
    c: Coincident(g2,g3)
    c: Coincident(g3,g0)
    c: Horizontal(g0)
    c: Horizontal(g2)
    c: Vertical(g3)
    c: DistanceX(g4) = 100
    c: Symmetric(g0,g0,g4)
    c: Symmetric(g0,g1,g-1)
    c: Distance(g1) = 80
    c: Distance(g2) = 10
FEATURE [PartDesign::Pad] Pad018
  Direction = (1,1,1)
  Length = 7
  Length2 = 100
  Profile = -> Sketch045
  Type = 0
FEATURE [Sketcher::SketchObject] Sketch046
  FullyConstrained = true
  MapMode = 5
  Placement = pos=(0,0,0) rot=(1,0,0;3.14159rad)
  Support = -> [Pad018]
  sketch-geometry (2):
    g0: Circle CenterX=100 CenterY=30 CenterZ=0 NormalX=0 NormalY=0 NormalZ=1 AngleXU=0 Radius=1.4
    g1: Circle CenterX=100 CenterY=-30 CenterZ=0 NormalX=0 NormalY=0 NormalZ=1 AngleXU=0 Radius=1.4
  constraints (5):
    c: Diameter(g0) = 2.8
    c: Equal(g0,g1)
    c: Symmetric(g1,g0,g-1)
    c: DistanceX(g0) = 100
    c: Distance(g1,g0) = 60
FEATURE [PartDesign::Pocket] Pocket026
  BaseFeature = -> Pad018
  Length = 8
  Length2 = 100
  Profile = -> Sketch046
  Type = 0
FEATURE [Sketcher::SketchObject] Sketch047
  FullyConstrained = false
  MapMode = 5
  Placement = pos=(0,-40,0) rot=(1,0,0;1.5708rad)
  Support = -> [Pocket026]
  sketch-geometry (2):
    g0: Circle CenterX=107.358 CenterY=3.5 CenterZ=0 NormalX=0 NormalY=0 NormalZ=1 AngleXU=0 Radius=3.5
    g1: Circle CenterX=92.4718 CenterY=3.5 CenterZ=0 NormalX=0 NormalY=0 NormalZ=1 AngleXU=0 Radius=3.5
  constraints (4):
    c: DistanceY(g0) = 3.5
    c: DistanceY(g1) = 3.5
    c: Diameter(g0) = 7
    c: Equal(g0,g1)
FEATURE [PartDesign::Pocket] Pocket027
  BaseFeature = -> Pocket026
  Length = 5
  Length2 = 100
  Profile = -> Sketch047
  Type = 1
FEATURE [PartDesign::Body] Body006  label="FanHandle"
  Group = -> [Sketch045,Pad018,Sketch046,Pocket026,Sketch047,Pocket027]
  Origin = -> Origin006
  Placement = pos=(0,0,36.5) rot=(0,0,1;0rad)
  Tip = -> Pocket027
FEATURE [Sketcher::SketchObject] Sketch049  label="Fillet"
  FullyConstrained = true
  MapMode = 5
  Placement = pos=(-9.5e-14,4.9e-14,40) rot=(0,0,-1;1.5708rad)
  sketch-geometry (3):
    g0: LineSegment StartX=-80.25 StartY=4.75736 StartZ=0 EndX=-76.0074 EndY=9 EndZ=0
    g1: LineSegment StartX=-76.0074 StartY=9 StartZ=0 EndX=-80.25 EndY=9 EndZ=0
    g2: LineSegment StartX=-80.25 StartY=9 StartZ=0 EndX=-80.25 EndY=4.75736 EndZ=0
  constraints (9):
    c: Coincident(g0,g1)
    c: Horizontal(g1)
    c: Coincident(g1,g2)
    c: Coincident(g2,g0)
    c: Vertical(g2)
    c: Angle(g0) = 0.785398
    c: DistanceY(g0) = 9
    c: Distance(g0) = 6
    c: DistanceX(g0) = -80.25
FEATURE [PartDesign::Mirrored] Mirrored003
  BaseFeature = -> Pad017
  MirrorPlane = -> Sketch044 [V_Axis]
  Originals = -> [Pad017]
  Placement = pos=(0,0,0) rot=(1,0,0;1.5708rad)
FEATURE [PartDesign::Chamfer] Chamfer025
  Angle = 45
  Base = -> Mirrored003 [Edge220,Edge74,Edge73,Edge197]
  BaseFeature = -> Mirrored003
  ChamferType = 0
  FlipDirection = false
  Placement = pos=(0,0,0) rot=(1,0,0;1.5708rad)
  Size = 1.5
  Size2 = 1
  SupportTransform = false
FEATURE [PartDesign::Body] Body003  label="Floor250x67"
  Group = -> [Sketch007,Pad004,Sketch015,Pocket007,Sketch032,Pad011,Sketch033,Mirrored,Pocket017,Sketch036,Pad013,Sketch037,Pocket019,MultiTransform001,LinearPattern002,Sketch044,Pad017,Mirrored003,Chamfer025]
  Origin = -> Origin003
  Placement = pos=(0,80,0) rot=(0,0,1;0rad)
  Tip = -> Chamfer025
FEATURE [Sketcher::SketchObject] Sketch050  label="sideNotches"
  FullyConstrained = true
  MapMode = 5
  Placement = pos=(-124,0,0) rot=(0.57735,-0.57735,-0.57735;2.0944rad)
  Support = -> [Pocket005]
  sketch-geometry (4):
    g0: LineSegment StartX=78 StartY=2 StartZ=0 EndX=80 EndY=2 EndZ=0
    g1: LineSegment StartX=80 StartY=2 StartZ=0 EndX=80 EndY=0 EndZ=0
    g2: LineSegment StartX=80 StartY=0 StartZ=0 EndX=78 EndY=0 EndZ=0
    g3: LineSegment StartX=78 StartY=0 StartZ=0 EndX=78 EndY=2 EndZ=0
  constraints (12):
    c: Coincident(g0,g1)
    c: Coincident(g1,g2)
    c: Coincident(g2,g3)
    c: Coincident(g3,g0)
    c: Horizontal(g0)
    c: Horizontal(g2)
    c: Vertical(g1)
    c: Vertical(g3)
    c: PointOnObject(g1,g-1)
    c: Distance(g3) = 2
    c: Distance(g0) = 2
    c: DistanceX(g1) = 80
FEATURE [PartDesign::Pocket] Pocket031
  BaseFeature = -> Pocket005
  Length = 5
  Length2 = 100
  Profile = -> Sketch050
  Type = 1
FEATURE [PartDesign::Mirrored] Mirrored004
  BaseFeature = -> Pocket031
  MirrorPlane = -> Sketch050 [V_Axis]
  Originals = -> [Pocket031]
FEATURE [PartDesign::Chamfer] Chamfer
  Angle = 45
  Base = -> Mirrored004 [Edge34]
  BaseFeature = -> Mirrored004
  ChamferType = 0
  FlipDirection = false
  Size = 2
  Size2 = 1
  SupportTransform = false
FEATURE [Sketcher::SketchObject] Sketch051  label="cornercuts"
  FullyConstrained = true
  MapMode = 5
  Placement = pos=(0,0,0) rot=(1,0,0;3.14159rad)
  sketch-geometry (6):
    g0: LineSegment StartX=-125 StartY=75.7574 StartZ=0 EndX=-120.757 EndY=80 EndZ=0
    g1: LineSegment StartX=-120.757 StartY=80 StartZ=0 EndX=-125 EndY=80 EndZ=0
    g2: LineSegment StartX=-125 StartY=80 StartZ=0 EndX=-125 EndY=75.7574 EndZ=0
    g3: LineSegment StartX=-120.757 StartY=-80 StartZ=0 EndX=-125 EndY=-75.7574 EndZ=0
    g4: LineSegment StartX=-125 StartY=-75.7574 StartZ=0 EndX=-125 EndY=-80 EndZ=0
    g5: LineSegment StartX=-125 StartY=-80 StartZ=0 EndX=-120.757 EndY=-80 EndZ=0
  constraints (18):
    c: Coincident(g0,g1)
    c: Horizontal(g1)
    c: Coincident(g1,g2)
    c: Coincident(g2,g0)
    c: Vertical(g2)
    c: Distance(g0) = 6
    c: Angle(g0) = 0.785398
    c: DistanceX(g1) = -125
    c: DistanceY(g1) = 80
    c: Coincident(g3,g4)
    c: Coincident(g4,g5)
    c: Coincident(g5,g3)
    c: Distance(g3) = 6
    c: Angle(g3) = 2.35619
    c: DistanceX(g4) = -125
    c: DistanceY(g4) = -80
    c: Vertical(g4)
    c: Horizontal(g5)
FEATURE [PartDesign::Pocket] Pocket033
  BaseFeature = -> Pocket012
  Length = 20
  Length2 = 100
  Placement = pos=(0,0,0) rot=(0.57735,0.57735,0.57735;2.0944rad)
  Profile = -> Sketch025
  Type = 0
FEATURE [PartDesign::Pocket] Pocket034
  BaseFeature = -> Pocket033
  Length = 17
  Length2 = 100
  Placement = pos=(0,0,0) rot=(0.57735,0.57735,0.57735;2.0944rad)
  Profile = -> Sketch026
  Type = 0
FEATURE [PartDesign::Pocket] Pocket035
  BaseFeature = -> Pocket034
  Length = 2
  Length2 = 100
  Placement = pos=(0,0,0) rot=(0.57735,0.57735,0.57735;2.0944rad)
  Profile = -> Sketch040
  Type = 0
FEATURE [PartDesign::Pad] Pad021
  BaseFeature = -> Pocket035
  Direction = (1,1,1)
  Length = 3
  Length2 = 100
  Placement = pos=(0,0,0) rot=(0.57735,0.57735,0.57735;2.0944rad)
  Profile = -> Sketch049
  Reversed = true
  Type = 0
FEATURE [PartDesign::Mirrored] Mirrored006
  BaseFeature = -> Pad021
  MirrorPlane = -> Sketch049 [V_Axis]
  Originals = -> [Pad021]
  Placement = pos=(0,0,0) rot=(0.57735,0.57735,0.57735;2.0944rad)
FEATURE [PartDesign::Chamfer] Chamfer030
  Angle = 45
  Base = -> Mirrored006 [Edge138,Edge38,Edge10,Edge12]
  BaseFeature = -> Mirrored006
  ChamferType = 0
  FlipDirection = false
  Placement = pos=(0,0,0) rot=(0.57735,0.57735,0.57735;2.0944rad)
  Size = 1
  Size2 = 1
  SupportTransform = false
FEATURE [PartDesign::Chamfer] Chamfer031
  Angle = 45
  Base = -> Chamfer030 [Face5]
  BaseFeature = -> Chamfer030
  ChamferType = 0
  FlipDirection = false
  Placement = pos=(0,0,0) rot=(0.57735,0.57735,0.57735;2.0944rad)
  Size = 1
  Size2 = 1
  SupportTransform = false
FEATURE [PartDesign::Chamfer] Chamfer032
  Angle = 45
  Base = -> Pocket025 [Edge4,Edge2,Edge54,Edge66]
  BaseFeature = -> Pocket025
  ChamferType = 0
  FlipDirection = false
  Size = 1.5
  Size2 = 1
  SupportTransform = false
FEATURE [PartDesign::Body] Body  label="MainPanel250x160"
  Group = -> [Sketch,Pad,Sketch001,Sketch002,Pad001,Pocket,Sketch019,Sketch021,Pocket009,Sketch022,Pocket010,Sketch043,Pocket025,Chamfer032]
  Origin = -> Origin
  Placement = pos=(0,0,-36.5) rot=(0,0,1;0rad)
  Tip = -> Chamfer032
FEATURE [PartDesign::Pocket] Pocket036
  BaseFeature = -> Pocket011
  Length = 2
  Length2 = 100
  Placement = pos=(0,0,0) rot=(0.57735,0.57735,0.57735;2.0944rad)
  Profile = -> Sketch039
  Type = 0
FEATURE [PartDesign::Chamfer] Chamfer033
  Angle = 45
  Base = -> Pocket036 [Edge1,Edge4,Edge8,Edge89,Edge11,Edge12,Edge9,Edge2]
  BaseFeature = -> Pocket036
  ChamferType = 0
  FlipDirection = false
  Placement = pos=(0,0,0) rot=(0.57735,0.57735,0.57735;2.0944rad)
  Size = 1
  Size2 = 1
  SupportTransform = false
FEATURE [PartDesign::Pocket] Pocket037
  BaseFeature = -> Chamfer
  Length = 5
  Length2 = 100
  Profile = -> Sketch051
  Type = 0
FEATURE [PartDesign::Chamfer] Chamfer034
  Angle = 45
  Base = -> Pocket037 [Edge65,Edge64]
  BaseFeature = -> Pocket037
  ChamferType = 0
  FlipDirection = false
  Size = 1.5
  Size2 = 1
  SupportTransform = false
FEATURE [PartDesign::Chamfer] Chamfer035
  Angle = 45
  Base = -> Chamfer034 [Edge37]
  BaseFeature = -> Chamfer034
  ChamferType = 0
  FlipDirection = false
  Size = 2
  Size2 = 1
  SupportTransform = false
FEATURE [Sketcher::SketchObject] Sketch056
  FullyConstrained = false
  MapMode = 5
  Placement = pos=(-8.49e-14,-76.5,8.4e-15) rot=(-0.57735,-0.57735,0.57735;4.18879rad)
  Support = -> [Chamfer033]
  sketch-geometry (3):
    g0: LineSegment StartX=-31.7643 StartY=4.39575 StartZ=0 EndX=-28.9845 EndY=7.5426 EndZ=0
    g1: LineSegment StartX=-28.9845 StartY=7.5426 StartZ=0 EndX=-32.2625 EndY=7.75239 EndZ=0
    g2: LineSegment StartX=-32.2625 StartY=7.75239 StartZ=0 EndX=-31.7643 EndY=4.39575 EndZ=0
  constraints (3):
    c: Coincident(g0,g1)
    c: Coincident(g1,g2)
    c: Coincident(g2,g0)
FEATURE [PartDesign::Pocket] Pocket038
  BaseFeature = -> Chamfer033
  Length = 154
  Length2 = 100
  Placement = pos=(0,0,0) rot=(0.57735,0.57735,0.57735;2.0944rad)
  Profile = -> Sketch056
  Type = 0
FEATURE [PartDesign::Body] Body004  label="DBEndPanel"
  Group = -> [Sketch008,Pad005,Sketch009,Pocket002,Sketch012,Sketch016,Pad007,Pocket008,Sketch023,Pocket011,Sketch039,Pocket036,Chamfer033,Sketch056,Pocket038]
  Origin = -> Origin004
  Placement = pos=(-128.5,0,0) rot=(0,0,1;0rad)
  Tip = -> Pocket038
FEATURE [Sketcher::SketchObject] Sketch057
  FullyConstrained = false
  MapMode = 5
  Placement = pos=(-3.65e-14,-83,1.83e-14) rot=(-0.57735,-0.57735,0.57735;4.18879rad)
  Support = -> [Chamfer031]
  sketch-geometry (3):
    g0: LineSegment StartX=-40.835 StartY=5.54707 StartZ=0 EndX=-36.6329 EndY=-0.347511 EndZ=0
    g1: LineSegment StartX=-36.6329 StartY=-0.347511 StartZ=0 EndX=-44.1032 EndY=-0.63932 EndZ=0
    g2: LineSegment StartX=-44.1032 StartY=-0.63932 StartZ=0 EndX=-40.835 EndY=5.54707 EndZ=0
  constraints (3):
    c: Coincident(g0,g1)
    c: Coincident(g1,g2)
    c: Coincident(g2,g0)
FEATURE [PartDesign::Pocket] Pocket039
  BaseFeature = -> Chamfer031
  Length = 5
  Length2 = 100
  Placement = pos=(0,0,0) rot=(0.57735,0.57735,0.57735;2.0944rad)
  Profile = -> Sketch057
  Type = 1
FEATURE [PartDesign::Body] Body001  label="VentEndPanel166x80"
  Group = -> [Sketch003,Sketch004,Pad002,Sketch005,Pocket001,Sketch011,Pocket003,MultiTransform,LinearPattern,LinearPattern001,Sketch024,Pocket012,Sketch025,Sketch026,Sketch040,Sketch049,Pocket033,Pocket034,Pocket035,Pad021,Mirrored006,Chamfer030,Chamfer031,Sketch057,Pocket039]
  Origin = -> Origin001
  Placement = pos=(116.5,0,0) rot=(0,0,1;0rad)
  Tip = -> Pocket039
FEATURE [PartDesign::Pocket] Pocket040
  BaseFeature = -> Pad012
  Length = 11
  Length2 = 100
  Placement = pos=(0,0,0) rot=(1,0,0;1.5708rad)
  Profile = -> Sketch038
  Type = 0
FEATURE [PartDesign::Pocket] Pocket041
  BaseFeature = -> Pocket040
  Length = 14
  Length2 = 100
  Placement = pos=(0,0,0) rot=(1,0,0;1.5708rad)
  Profile = -> Sketch030
  Type = 0
FEATURE [PartDesign::Pad] Pad022
  BaseFeature = -> Pocket041
  Direction = (1,1,1)
  Length = 7
  Length2 = 100
  Placement = pos=(0,0,0) rot=(1,0,0;1.5708rad)
  Profile = -> Sketch041
  Type = 0
FEATURE [PartDesign::Pad] Pad023
  BaseFeature = -> Pad022
  Direction = (1,1,1)
  Length = 250
  Length2 = 100
  Placement = pos=(0,0,0) rot=(1,0,0;1.5708rad)
  Profile = -> Sketch042
  Reversed = true
  Type = 0
FEATURE [PartDesign::Mirrored] Mirrored007
  BaseFeature = -> Pad023
  MirrorPlane = -> Sketch042 [V_Axis]
  Originals = -> [Pad023]
  Placement = pos=(0,0,0) rot=(1,0,0;1.5708rad)
FEATURE [PartDesign::Chamfer] Chamfer036
  Angle = 45
  Base = -> Mirrored007 [Edge102,Edge100,Edge98,Edge95,Edge149,Edge123,Edge122,Edge128]
  BaseFeature = -> Mirrored007
  ChamferType = 0
  FlipDirection = false
  Placement = pos=(0,0,0) rot=(1,0,0;1.5708rad)
  Size = 1.5
  Size2 = 1
  SupportTransform = false
FEATURE [PartDesign::Body] Body002  label="Top250x67"
  Group = -> [Sketch006,Pad003,Sketch014,Pocket006,Sketch029,Pad010,Sketch030,Sketch034,Pad012,Sketch038,Sketch041,Sketch042,Pocket040,Pocket041,Pad022,Pad023,Mirrored007,Chamfer036]
  Origin = -> Origin002
  Placement = pos=(0,-77,0) rot=(0,0,1;0rad)
  Tip = -> Chamfer036
FEATURE [Sketcher::SketchObject] Sketch058
  FullyConstrained = true
  MapMode = 5
  Placement = pos=(0,0,0) rot=(1,0,0;3.14159rad)
  Support = -> [Chamfer035]
  sketch-geometry (8):
    g0: Circle CenterX=50 CenterY=25 CenterZ=0 NormalX=0 NormalY=0 NormalZ=1 AngleXU=0 Radius=3
    g1: Circle CenterX=78 CenterY=25 CenterZ=0 NormalX=0 NormalY=0 NormalZ=1 AngleXU=0 Radius=3
    g2: Circle CenterX=50 CenterY=-25 CenterZ=0 NormalX=0 NormalY=0 NormalZ=1 AngleXU=0 Radius=3
    g3: Circle CenterX=78 CenterY=-25 CenterZ=0 NormalX=0 NormalY=0 NormalZ=1 AngleXU=0 Radius=3
    g4: LineSegment StartX=50 StartY=25 StartZ=0 EndX=78 EndY=25 EndZ=0
    g5: LineSegment StartX=78 StartY=-25 StartZ=0 EndX=50 EndY=-25 EndZ=0
    g6: LineSegment StartX=50 StartY=25 StartZ=0 EndX=50 EndY=-25 EndZ=0
    g7: LineSegment StartX=78 StartY=25 StartZ=0 EndX=78 EndY=-25 EndZ=0
  constraints (19):
    c: Coincident(g4,g0)
    c: Coincident(g4,g1)
    c: Coincident(g5,g3)
    c: Coincident(g5,g2)
    c: Coincident(g6,g0)
    c: Coincident(g6,g2)
    c: Coincident(g7,g1)
    c: Coincident(g7,g3)
    c: Equal(g6,g7)
    c: Distance(g6) = 50
    c: Distance(g4) = 28
    c: Horizontal(g4)
    c: Equal(g5,g4)
    c: Diameter(g0) = 6
    c: Equal(g0,g1)
    c: Equal(g0,g2)
    c: Equal(g0,g3)
    c: Symmetric(g2,g0,g-1)
    c: Distance(g-1,g6) = 50
FEATURE [PartDesign::Pad] Pad024
  BaseFeature = -> Chamfer035
  Direction = (1,1,1)
  Length = 3
  Length2 = 100
  Profile = -> Sketch058
  Type = 0
FEATURE [Sketcher::SketchObject] Sketch059
  FullyConstrained = true
  MapMode = 5
  Placement = pos=(0,0,-3) rot=(1,0,0;3.14159rad)
  Support = -> [Pad024]
  sketch-geometry (4):
    g0: Circle CenterX=50 CenterY=25 CenterZ=0 NormalX=0 NormalY=0 NormalZ=1 AngleXU=0 Radius=1.4
    g1: Circle CenterX=78 CenterY=25 CenterZ=0 NormalX=0 NormalY=0 NormalZ=1 AngleXU=0 Radius=1.4
    g2: Circle CenterX=50 CenterY=-25 CenterZ=0 NormalX=0 NormalY=0 NormalZ=1 AngleXU=0 Radius=1.4
    g3: Circle CenterX=78 CenterY=-25 CenterZ=0 NormalX=0 NormalY=0 NormalZ=1 AngleXU=0 Radius=1.4
  constraints (10):
    c: Symmetric(g2,g0,g-1)
    c: Symmetric(g3,g1,g-1)
    c: DistanceX(g0) = 50
    c: Distance(g1,g0) = 28
    c: Diameter(g0) = 2.8
    c: Equal(g0,g1)
    c: Equal(g0,g3)
    c: Equal(g0,g2)
    c: Distance(g3,g1) = 50
    c: Distance(g2,g0) = 50
FEATURE [PartDesign::Pocket] Pocket042
  BaseFeature = -> Pad024
  Length = 5
  Length2 = 100
  Profile = -> Sketch059
  Type = 0
FEATURE [PartDesign::Body] Body005  label="FanPanel"
  Group = -> [Sketch010,Pad006,Sketch013,Pocket005,Sketch050,Pocket031,Mirrored004,Chamfer,Sketch051,Pocket037,Chamfer034,Chamfer035,Sketch058,Pad024,Sketch059,Pocket042]
  Origin = -> Origin005
  Placement = pos=(0,0,32.5) rot=(0,0,1;3.14159rad)
  Tip = -> Pocket042
FEATURE [Mesh::Feature] Mesh  label="Pocket042 (Meshed)"
FEATURE [Mesh::Feature] Mesh001  label="Chamfer032 (Meshed)"
FEATURE [Mesh::Feature] Mesh002  label="Pocket039 (Meshed)"
FEATURE [Mesh::Feature] Mesh003  label="Chamfer036 (Meshed)"
FEATURE [Mesh::Feature] Mesh004  label="Chamfer025 (Meshed)"
FEATURE [Mesh::Feature] Mesh005  label="Pocket038 (Meshed)"
FEATURE [Mesh::Feature] Mesh006  label="Pocket042 (Meshed)001"
FEATURE [Mesh::Feature] Mesh007  label="Pocket027 (Meshed)"
